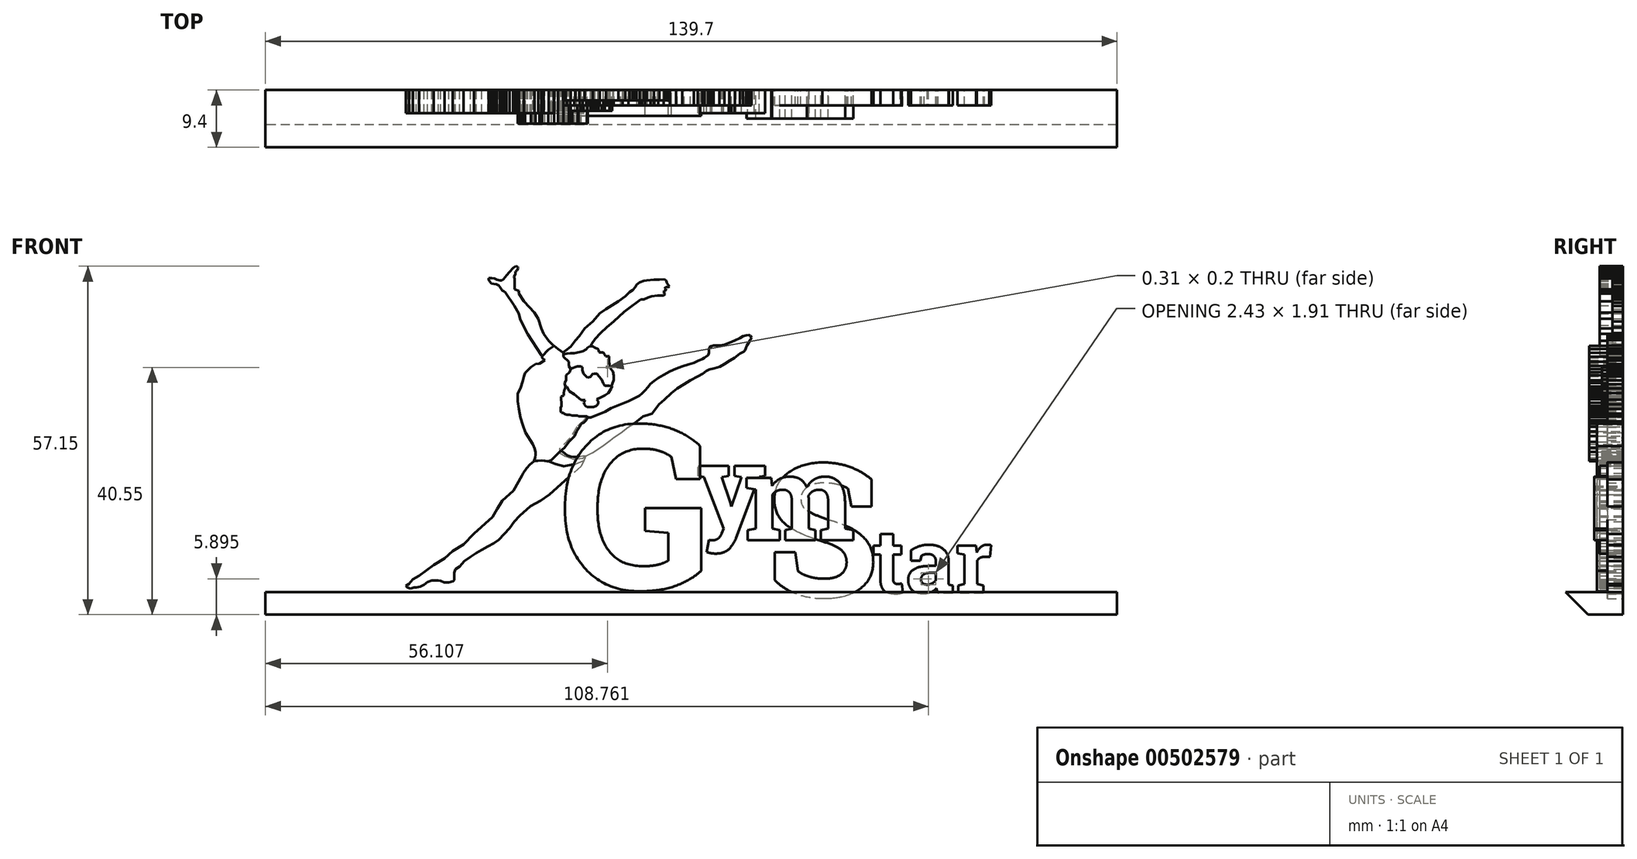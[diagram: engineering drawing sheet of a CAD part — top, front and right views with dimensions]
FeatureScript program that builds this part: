
annotation { "Feature Type Name" : "Feature", "Feature Type Description" : "" }
export const myFeature = defineFeature(function(context is Context, id is Id, definition is map)
    precondition{}
    {
        {
            var Q0;
            Q0=qCreatedBy(makeId("Front.planeOp"),FACE);
            var sketch = newSketch(context, id + "F0", { "sketchPlane" : qUnion([Q0])});
            skLineSegment(sketch, "E0", {"start": v(-43.44, 2.65) * mm, "end": v(-42.3, 3.36) * mm});
            skLineSegment(sketch, "E1", {"start": v(-42.3, 3.36) * mm, "end": v(-39.46, 5.47) * mm});
            skLineSegment(sketch, "E2", {"start": v(-39.46, 5.47) * mm, "end": v(-37.36, 6.73) * mm});
            skLineSegment(sketch, "E3", {"start": v(-37.36, 6.73) * mm, "end": v(-35.78, 8.1) * mm});
            skLineSegment(sketch, "E4", {"start": v(-35.78, 8.1) * mm, "end": v(-33.68, 9.35) * mm});
            skLineSegment(sketch, "E5", {"start": v(-33.68, 9.35) * mm, "end": v(-31.69, 11.46) * mm});
            skLineSegment(sketch, "E6", {"start": v(-31.69, 11.46) * mm, "end": v(-29.58, 13.35) * mm});
            skLineSegment(sketch, "E7", {"start": v(-29.58, 13.35) * mm, "end": v(-28.1, 14.68) * mm});
            skLineSegment(sketch, "E8", {"start": v(-28.1, 14.68) * mm, "end": v(-27.2, 16.26) * mm});
            skLineSegment(sketch, "E9", {"start": v(-27.2, 16.26) * mm, "end": v(-26.68, 17.07) * mm});
            skLineSegment(sketch, "E10", {"start": v(-26.68, 17.07) * mm, "end": v(-26.22, 17.82) * mm});
            skLineSegment(sketch, "E11", {"start": v(-26.22, 17.82) * mm, "end": v(-25.58, 18.4) * mm});
            skLineSegment(sketch, "E12", {"start": v(-25.58, 18.4) * mm, "end": v(-25.2, 18.74) * mm});
            skLineSegment(sketch, "E13", {"start": v(-25.2, 18.74) * mm, "end": v(-24.43, 19.43) * mm});
            skLineSegment(sketch, "E14", {"start": v(-24.43, 19.43) * mm, "end": v(-24.01, 19.8) * mm});
            skLineSegment(sketch, "E15", {"start": v(-24.01, 19.8) * mm, "end": v(-22.43, 22.66) * mm});
            skLineSegment(sketch, "E16", {"start": v(-22.43, 22.66) * mm, "end": v(-22.17, 23.15) * mm});
            skLineSegment(sketch, "E17", {"start": v(-22.17, 23.15) * mm, "end": v(-21.53, 24.13) * mm});
            skLineSegment(sketch, "E18", {"start": v(-21.53, 24.13) * mm, "end": v(-20.84, 24.84) * mm});
            skLineSegment(sketch, "E19", {"start": v(-20.84, 24.84) * mm, "end": v(-20.54, 25.1) * mm});
            skLineSegment(sketch, "E20", {"start": v(-20.54, 25.1) * mm, "end": v(-20.08, 25.48) * mm});
            skLineSegment(sketch, "E21", {"start": v(-20.08, 25.48) * mm, "end": v(-18.63, 25.62) * mm});
            skLineSegment(sketch, "E22", {"start": v(-18.63, 25.62) * mm, "end": v(-17.07, 25.4) * mm});
            skLineSegment(sketch, "E23", {"start": v(-17.07, 25.4) * mm, "end": v(-16, 24.93) * mm});
            skLineSegment(sketch, "E24", {"start": v(-16, 24.93) * mm, "end": v(-14.36, 24.49) * mm});
            skLineSegment(sketch, "E25", {"start": v(-14.36, 24.49) * mm, "end": v(-12.24, 24.89) * mm});
            skLineSegment(sketch, "E26", {"start": v(-12.24, 24.89) * mm, "end": v(-10.47, 25.6) * mm});
            skLineSegment(sketch, "E27", {"start": v(-10.47, 25.6) * mm, "end": v(-11, 24.49) * mm});
            skLineSegment(sketch, "E28", {"start": v(-11, 24.49) * mm, "end": v(-12.41, 23.21) * mm});
            skLineSegment(sketch, "E29", {"start": v(-12.41, 23.21) * mm, "end": v(-13.58, 22.17) * mm});
            skLineSegment(sketch, "E30", {"start": v(-13.58, 22.17) * mm, "end": v(-15.14, 20.76) * mm});
            skLineSegment(sketch, "E31", {"start": v(-15.14, 20.76) * mm, "end": v(-17.1, 19) * mm});
            skLineSegment(sketch, "E32", {"start": v(-17.1, 19) * mm, "end": v(-18.82, 17.82) * mm});
            skLineSegment(sketch, "E33", {"start": v(-18.82, 17.82) * mm, "end": v(-20.76, 16.8) * mm});
            skLineSegment(sketch, "E34", {"start": v(-20.76, 16.8) * mm, "end": v(-21.82, 15.85) * mm});
            skLineSegment(sketch, "E35", {"start": v(-21.82, 15.85) * mm, "end": v(-22.88, 14.9) * mm});
            skLineSegment(sketch, "E36", {"start": v(-22.88, 14.9) * mm, "end": v(-23.88, 13.8) * mm});
            skLineSegment(sketch, "E37", {"start": v(-23.88, 13.8) * mm, "end": v(-24.82, 12.54) * mm});
            skLineSegment(sketch, "E38", {"start": v(-24.82, 12.54) * mm, "end": v(-26.1, 11.12) * mm});
            skLineSegment(sketch, "E39", {"start": v(-26.1, 11.12) * mm, "end": v(-26.87, 10.26) * mm});
            skLineSegment(sketch, "E40", {"start": v(-26.87, 10.26) * mm, "end": v(-27.87, 9.62) * mm});
            skLineSegment(sketch, "E41", {"start": v(-27.87, 9.62) * mm, "end": v(-29, 9.01) * mm});
            skLineSegment(sketch, "E42", {"start": v(-29, 9.01) * mm, "end": v(-30.2, 8.3) * mm});
            skLineSegment(sketch, "E43", {"start": v(-30.2, 8.3) * mm, "end": v(-31.18, 7.72) * mm});
            skLineSegment(sketch, "E44", {"start": v(-31.18, 7.72) * mm, "end": v(-32.32, 6.97) * mm});
            skLineSegment(sketch, "E45", {"start": v(-32.32, 6.97) * mm, "end": v(-33.51, 6.16) * mm});
            skLineSegment(sketch, "E46", {"start": v(-33.51, 6.16) * mm, "end": v(-34.44, 5.13) * mm});
            skLineSegment(sketch, "E47", {"start": v(-34.44, 5.13) * mm, "end": v(-35.24, 4.6) * mm});
            skLineSegment(sketch, "E48", {"start": v(-35.24, 4.6) * mm, "end": v(-35.44, 3.95) * mm});
            skLineSegment(sketch, "E49", {"start": v(-35.44, 3.95) * mm, "end": v(-35.44, 3.14) * mm});
            skLineSegment(sketch, "E50", {"start": v(-35.44, 3.14) * mm, "end": v(-35.44, 2.54) * mm});
            skLineSegment(sketch, "E51", {"start": v(-35.44, 2.54) * mm, "end": v(-35.7, 2.26) * mm});
            skLineSegment(sketch, "E52", {"start": v(-35.7, 2.26) * mm, "end": v(-36.52, 2.1) * mm});
            skLineSegment(sketch, "E53", {"start": v(-36.52, 2.1) * mm, "end": v(-37.41, 2.1) * mm});
            skLineSegment(sketch, "E54", {"start": v(-37.41, 2.1) * mm, "end": v(-38.1, 2.34) * mm});
            skLineSegment(sketch, "E55", {"start": v(-38.1, 2.34) * mm, "end": v(-38.52, 2.42) * mm});
            skLineSegment(sketch, "E56", {"start": v(-38.52, 2.42) * mm, "end": v(-39.84, 2.42) * mm});
            skLineSegment(sketch, "E57", {"start": v(-39.84, 2.42) * mm, "end": v(-40.65, 2.17) * mm});
            skLineSegment(sketch, "E58", {"start": v(-40.65, 2.17) * mm, "end": v(-41.32, 1.6) * mm});
            skLineSegment(sketch, "E59", {"start": v(-41.32, 1.6) * mm, "end": v(-42.07, 1.22) * mm});
            skLineSegment(sketch, "E60", {"start": v(-42.07, 1.22) * mm, "end": v(-42.82, 1.13) * mm});
            skLineSegment(sketch, "E61", {"start": v(-42.82, 1.13) * mm, "end": v(-43.27, 1.13) * mm});
            skLineSegment(sketch, "E62", {"start": v(-43.27, 1.13) * mm, "end": v(-43.93, 0.89) * mm});
            skLineSegment(sketch, "E63", {"start": v(-43.93, 0.89) * mm, "end": v(-44.5, 1.07) * mm});
            skLineSegment(sketch, "E64", {"start": v(-44.5, 1.07) * mm, "end": v(-44.84, 1.38) * mm});
            skLineSegment(sketch, "E65", {"start": v(-44.84, 1.38) * mm, "end": v(-44.24, 1.76) * mm});
            skLineSegment(sketch, "E66", {"start": v(-44.24, 1.76) * mm, "end": v(-43.92, 2.12) * mm});
            skLineSegment(sketch, "E67", {"start": v(-43.92, 2.12) * mm, "end": v(-43.44, 2.65) * mm});
            skSolve(sketch);
        }
        {
            var Q0;
            Q0 = qSketchRegion(id + "F0", true);
            extrude(context, id + "F1", {"entities" : qUnion([Q0]), "depth" : 4.5 * mm, "offsetDistance" : 25 * mm});
        }
        {
            var Q0;
            Q0=qCreatedBy(makeId("Front.planeOp"),FACE);
            var sketch = newSketch(context, id + "F2", { "sketchPlane" : qUnion([Q0])});
            skLineSegment(sketch, "E68", {"start": v(-19.86, 26.12) * mm, "end": v(-20.1, 25.49) * mm});
            skLineSegment(sketch, "E69", {"start": v(-20.1, 25.49) * mm, "end": v(-18.62, 25.63) * mm});
            skLineSegment(sketch, "E70", {"start": v(-18.62, 25.63) * mm, "end": v(-17.22, 25.42) * mm});
            skLineSegment(sketch, "E71", {"start": v(-17.22, 25.42) * mm, "end": v(-16.72, 25.64) * mm});
            skLineSegment(sketch, "E72", {"start": v(-16.72, 25.64) * mm, "end": v(-15.68, 26.7) * mm});
            skLineSegment(sketch, "E73", {"start": v(-15.68, 26.7) * mm, "end": v(-15.16, 27.23) * mm});
            skLineSegment(sketch, "E74", {"start": v(-15.16, 27.23) * mm, "end": v(-14.2, 28.04) * mm});
            skLineSegment(sketch, "E75", {"start": v(-14.2, 28.04) * mm, "end": v(-13.4, 29.18) * mm});
            skLineSegment(sketch, "E76", {"start": v(-13.4, 29.18) * mm, "end": v(-12.27, 30.32) * mm});
            skLineSegment(sketch, "E77", {"start": v(-12.27, 30.32) * mm, "end": v(-11.84, 31.22) * mm});
            skLineSegment(sketch, "E78", {"start": v(-11.84, 31.22) * mm, "end": v(-11.3, 32.07) * mm});
            skLineSegment(sketch, "E79", {"start": v(-11.3, 32.07) * mm, "end": v(-11, 32.66) * mm});
            skLineSegment(sketch, "E80", {"start": v(-11, 32.66) * mm, "end": v(-10.47, 32.92) * mm});
            skLineSegment(sketch, "E81", {"start": v(-10.47, 32.92) * mm, "end": v(-10, 33.4) * mm});
            skLineSegment(sketch, "E82", {"start": v(-10, 33.4) * mm, "end": v(-9.71, 33.95) * mm});
            skLineSegment(sketch, "E83", {"start": v(-9.71, 33.95) * mm, "end": v(-9.86, 34.1) * mm});
            skLineSegment(sketch, "E84", {"start": v(-9.86, 34.1) * mm, "end": v(-10.68, 34.1) * mm});
            skLineSegment(sketch, "E85", {"start": v(-10.68, 34.1) * mm, "end": v(-11.46, 34.1) * mm});
            skLineSegment(sketch, "E86", {"start": v(-11.46, 34.1) * mm, "end": v(-11.6, 34.3) * mm});
            skLineSegment(sketch, "E87", {"start": v(-11.6, 34.3) * mm, "end": v(-12.13, 34.3) * mm});
            skLineSegment(sketch, "E88", {"start": v(-12.13, 34.3) * mm, "end": v(-12.65, 34.3) * mm});
            skLineSegment(sketch, "E89", {"start": v(-12.65, 34.3) * mm, "end": v(-13.18, 34.4) * mm});
            skLineSegment(sketch, "E90", {"start": v(-13.18, 34.4) * mm, "end": v(-13.7, 34.4) * mm});
            skLineSegment(sketch, "E91", {"start": v(-13.7, 34.4) * mm, "end": v(-14.15, 34.57) * mm});
            skLineSegment(sketch, "E92", {"start": v(-14.15, 34.57) * mm, "end": v(-14.38, 34.8) * mm});
            skLineSegment(sketch, "E93", {"start": v(-14.38, 34.8) * mm, "end": v(-14.77, 34.8) * mm});
            skLineSegment(sketch, "E94", {"start": v(-14.77, 34.8) * mm, "end": v(-14.91, 35.07) * mm});
            skLineSegment(sketch, "E95", {"start": v(-14.91, 35.07) * mm, "end": v(-14.91, 35.36) * mm});
            skLineSegment(sketch, "E96", {"start": v(-14.91, 35.36) * mm, "end": v(-14.97, 35.78) * mm});
            skLineSegment(sketch, "E97", {"start": v(-14.97, 35.78) * mm, "end": v(-14.76, 36.17) * mm});
            skLineSegment(sketch, "E98", {"start": v(-14.76, 36.17) * mm, "end": v(-14.76, 36.76) * mm});
            skLineSegment(sketch, "E99", {"start": v(-14.76, 36.76) * mm, "end": v(-14.88, 37.43) * mm});
            skLineSegment(sketch, "E100", {"start": v(-14.88, 37.43) * mm, "end": v(-14.88, 37.9) * mm});
            skLineSegment(sketch, "E101", {"start": v(-14.88, 37.9) * mm, "end": v(-14.37, 38.18) * mm});
            skLineSegment(sketch, "E102", {"start": v(-14.37, 38.18) * mm, "end": v(-14.32, 38.57) * mm});
            skLineSegment(sketch, "E103", {"start": v(-14.32, 38.57) * mm, "end": v(-14.3, 39.12) * mm});
            skLineSegment(sketch, "E104", {"start": v(-14.3, 39.12) * mm, "end": v(-14.12, 39.44) * mm});
            skLineSegment(sketch, "E105", {"start": v(-14.12, 39.44) * mm, "end": v(-14.04, 39.87) * mm});
            skLineSegment(sketch, "E106", {"start": v(-14.04, 39.87) * mm, "end": v(-14.18, 40.57) * mm});
            skLineSegment(sketch, "E107", {"start": v(-14.18, 40.57) * mm, "end": v(-13.85, 41.07) * mm});
            skLineSegment(sketch, "E108", {"start": v(-13.85, 41.07) * mm, "end": v(-13.85, 42.04) * mm});
            skLineSegment(sketch, "E109", {"start": v(-13.85, 42.04) * mm, "end": v(-13.2, 42.65) * mm});
            skLineSegment(sketch, "E110", {"start": v(-13.2, 42.65) * mm, "end": v(-13, 43.26) * mm});
            skLineSegment(sketch, "E111", {"start": v(-13, 43.26) * mm, "end": v(-13.35, 43.82) * mm});
            skLineSegment(sketch, "E112", {"start": v(-13.35, 43.82) * mm, "end": v(-13.35, 44.62) * mm});
            skLineSegment(sketch, "E113", {"start": v(-13.35, 44.62) * mm, "end": v(-14.41, 45.66) * mm});
            skLineSegment(sketch, "E114", {"start": v(-14.41, 45.66) * mm, "end": v(-14.41, 46.4) * mm});
            skLineSegment(sketch, "E115", {"start": v(-14.41, 46.4) * mm, "end": v(-15.48, 47.12) * mm});
            skLineSegment(sketch, "E116", {"start": v(-15.48, 47.12) * mm, "end": v(-16.2, 47.68) * mm});
            skLineSegment(sketch, "E117", {"start": v(-16.2, 47.68) * mm, "end": v(-17.3, 46.98) * mm});
            skLineSegment(sketch, "E118", {"start": v(-17.3, 46.98) * mm, "end": v(-18.52, 45.73) * mm});
            skLineSegment(sketch, "E119", {"start": v(-18.52, 45.73) * mm, "end": v(-18.52, 45.4) * mm});
            skLineSegment(sketch, "E120", {"start": v(-18.52, 45.4) * mm, "end": v(-18.03, 44.92) * mm});
            skLineSegment(sketch, "E121", {"start": v(-18.03, 44.92) * mm, "end": v(-19.03, 44.28) * mm});
            skLineSegment(sketch, "E122", {"start": v(-19.03, 44.28) * mm, "end": v(-19.82, 44.17) * mm});
            skLineSegment(sketch, "E123", {"start": v(-19.82, 44.17) * mm, "end": v(-20.68, 43.62) * mm});
            skLineSegment(sketch, "E124", {"start": v(-20.68, 43.62) * mm, "end": v(-21.27, 43.02) * mm});
            skLineSegment(sketch, "E125", {"start": v(-21.27, 43.02) * mm, "end": v(-21.82, 42.45) * mm});
            skLineSegment(sketch, "E126", {"start": v(-21.82, 42.45) * mm, "end": v(-22.03, 41.83) * mm});
            skLineSegment(sketch, "E127", {"start": v(-22.03, 41.83) * mm, "end": v(-22.26, 40.93) * mm});
            skLineSegment(sketch, "E128", {"start": v(-22.26, 40.93) * mm, "end": v(-22.68, 39.5) * mm});
            skLineSegment(sketch, "E129", {"start": v(-22.68, 39.5) * mm, "end": v(-23.19, 38.52) * mm});
            skLineSegment(sketch, "E130", {"start": v(-23.19, 38.52) * mm, "end": v(-23.19, 37.04) * mm});
            skLineSegment(sketch, "E131", {"start": v(-23.19, 37.04) * mm, "end": v(-23.03, 35.52) * mm});
            skLineSegment(sketch, "E132", {"start": v(-23.03, 35.52) * mm, "end": v(-22.68, 33.92) * mm});
            skLineSegment(sketch, "E133", {"start": v(-22.68, 33.92) * mm, "end": v(-22.26, 32.45) * mm});
            skLineSegment(sketch, "E134", {"start": v(-22.26, 32.45) * mm, "end": v(-21.73, 30.96) * mm});
            skLineSegment(sketch, "E135", {"start": v(-21.73, 30.96) * mm, "end": v(-21.13, 30.03) * mm});
            skLineSegment(sketch, "E136", {"start": v(-21.13, 30.03) * mm, "end": v(-20.32, 28.75) * mm});
            skLineSegment(sketch, "E137", {"start": v(-20.32, 28.75) * mm, "end": v(-19.97, 27.84) * mm});
            skLineSegment(sketch, "E138", {"start": v(-19.97, 27.84) * mm, "end": v(-19.78, 27.2) * mm});
            skLineSegment(sketch, "E139", {"start": v(-19.78, 27.2) * mm, "end": v(-19.78, 26.7) * mm});
            skLineSegment(sketch, "E140", {"start": v(-19.78, 26.7) * mm, "end": v(-19.86, 26.12) * mm});
            skSolve(sketch);
        }
        {
            var Q0;
            Q0 = qSketchRegion(id + "F2", true);
            extrude(context, id + "F3", {"entities" : qUnion([Q0]), "depth" : 6.5 * mm, "offsetDistance" : 25 * mm});
        }
        {
            var Q0;
            Q0=qCreatedBy(makeId("Front.planeOp"),FACE);
            var sketch = newSketch(context, id + "F4", { "sketchPlane" : qUnion([Q0])});
            skLineSegment(sketch, "E141", {"start": v(-10.44, 25.62) * mm, "end": v(-10.18, 26.15) * mm});
            skLineSegment(sketch, "E142", {"start": v(-10.18, 26.15) * mm, "end": v(-10.18, 26.4) * mm});
            skLineSegment(sketch, "E143", {"start": v(-10.18, 26.4) * mm, "end": v(-10.64, 26.4) * mm});
            skLineSegment(sketch, "E144", {"start": v(-10.64, 26.4) * mm, "end": v(-11.44, 26.25) * mm});
            skLineSegment(sketch, "E145", {"start": v(-11.44, 26.25) * mm, "end": v(-12.48, 26.25) * mm});
            skLineSegment(sketch, "E146", {"start": v(-12.48, 26.25) * mm, "end": v(-13.02, 26.35) * mm});
            skLineSegment(sketch, "E147", {"start": v(-13.02, 26.35) * mm, "end": v(-13.65, 26.6) * mm});
            skLineSegment(sketch, "E148", {"start": v(-13.65, 26.6) * mm, "end": v(-14.1, 26.98) * mm});
            skLineSegment(sketch, "E149", {"start": v(-14.1, 26.98) * mm, "end": v(-14.67, 27.36) * mm});
            skLineSegment(sketch, "E150", {"start": v(-14.67, 27.36) * mm, "end": v(-14.84, 27.5) * mm});
            skLineSegment(sketch, "E151", {"start": v(-14.84, 27.5) * mm, "end": v(-15.4, 27) * mm});
            skLineSegment(sketch, "E152", {"start": v(-15.4, 27) * mm, "end": v(-15.88, 26.48) * mm});
            skLineSegment(sketch, "E153", {"start": v(-15.88, 26.48) * mm, "end": v(-16.21, 26.2) * mm});
            skLineSegment(sketch, "E154", {"start": v(-16.21, 26.2) * mm, "end": v(-16.51, 25.86) * mm});
            skLineSegment(sketch, "E155", {"start": v(-16.51, 25.86) * mm, "end": v(-16.76, 25.65) * mm});
            skLineSegment(sketch, "E156", {"start": v(-16.76, 25.65) * mm, "end": v(-17.26, 25.43) * mm});
            skLineSegment(sketch, "E157", {"start": v(-17.26, 25.43) * mm, "end": v(-16.9, 25.29) * mm});
            skLineSegment(sketch, "E158", {"start": v(-16.9, 25.29) * mm, "end": v(-16.22, 24.96) * mm});
            skLineSegment(sketch, "E159", {"start": v(-16.22, 24.96) * mm, "end": v(-15.1, 24.62) * mm});
            skLineSegment(sketch, "E160", {"start": v(-15.1, 24.62) * mm, "end": v(-14.06, 24.47) * mm});
            skLineSegment(sketch, "E161", {"start": v(-14.06, 24.47) * mm, "end": v(-12.94, 24.64) * mm});
            skLineSegment(sketch, "E162", {"start": v(-12.94, 24.64) * mm, "end": v(-12.18, 24.84) * mm});
            skLineSegment(sketch, "E163", {"start": v(-12.18, 24.84) * mm, "end": v(-11.5, 25.14) * mm});
            skLineSegment(sketch, "E164", {"start": v(-11.5, 25.14) * mm, "end": v(-10.48, 25.57) * mm});
            skLineSegment(sketch, "E165", {"start": v(-10.44, 25.62) * mm, "end": v(-10.48, 25.57) * mm});
            skSolve(sketch);
        }
        {
            var Q0;
            Q0 = qSketchRegion(id + "F4", true);
            extrude(context, id + "F5", {"entities" : qUnion([Q0]), "depth" : 4 * mm, "offsetDistance" : 25 * mm});
        }
        {
            var Q0;
            Q0=qCreatedBy(makeId("Front.planeOp"),FACE);
            var sketch = newSketch(context, id + "F6", { "sketchPlane" : qUnion([Q0])});
            skLineSegment(sketch, "E166", {"start": v(-10.04, 26.5) * mm, "end": v(-8.77, 27.13) * mm});
            skLineSegment(sketch, "E167", {"start": v(-8.77, 27.13) * mm, "end": v(-7.76, 27.75) * mm});
            skLineSegment(sketch, "E168", {"start": v(-7.76, 27.75) * mm, "end": v(-6.54, 28.62) * mm});
            skLineSegment(sketch, "E169", {"start": v(-6.54, 28.62) * mm, "end": v(-5.36, 29.46) * mm});
            skLineSegment(sketch, "E170", {"start": v(-5.36, 29.46) * mm, "end": v(-4.62, 30.06) * mm});
            skLineSegment(sketch, "E171", {"start": v(-4.62, 30.06) * mm, "end": v(-3.31, 30.9) * mm});
            skLineSegment(sketch, "E172", {"start": v(-3.31, 30.9) * mm, "end": v(-1.95, 32.03) * mm});
            skLineSegment(sketch, "E173", {"start": v(-1.95, 32.03) * mm, "end": v(-0.18, 33.11) * mm});
            skLineSegment(sketch, "E174", {"start": v(-0.18, 33.11) * mm, "end": v(1, 34.08) * mm});
            skLineSegment(sketch, "E175", {"start": v(1, 34.08) * mm, "end": v(1.81, 34.35) * mm});
            skLineSegment(sketch, "E176", {"start": v(1.81, 34.35) * mm, "end": v(2.7, 34.66) * mm});
            skLineSegment(sketch, "E177", {"start": v(2.7, 34.66) * mm, "end": v(3.36, 35.56) * mm});
            skLineSegment(sketch, "E178", {"start": v(3.36, 35.56) * mm, "end": v(4.07, 36.45) * mm});
            skLineSegment(sketch, "E179", {"start": v(4.07, 36.45) * mm, "end": v(5.1, 37.3) * mm});
            skLineSegment(sketch, "E180", {"start": v(5.1, 37.3) * mm, "end": v(6.45, 38.61) * mm});
            skLineSegment(sketch, "E181", {"start": v(6.45, 38.61) * mm, "end": v(7.52, 39.49) * mm});
            skLineSegment(sketch, "E182", {"start": v(7.52, 39.49) * mm, "end": v(8.89, 40.32) * mm});
            skLineSegment(sketch, "E183", {"start": v(8.89, 40.32) * mm, "end": v(10.13, 41.05) * mm});
            skLineSegment(sketch, "E184", {"start": v(10.13, 41.05) * mm, "end": v(11.54, 41.79) * mm});
            skLineSegment(sketch, "E185", {"start": v(11.54, 41.79) * mm, "end": v(12.5, 42.35) * mm});
            skLineSegment(sketch, "E186", {"start": v(12.5, 42.35) * mm, "end": v(13.13, 42.87) * mm});
            skLineSegment(sketch, "E187", {"start": v(13.13, 42.87) * mm, "end": v(13.77, 43.15) * mm});
            skLineSegment(sketch, "E188", {"start": v(13.77, 43.15) * mm, "end": v(14.72, 43.37) * mm});
            skLineSegment(sketch, "E189", {"start": v(14.72, 43.37) * mm, "end": v(15.74, 43.65) * mm});
            skLineSegment(sketch, "E190", {"start": v(15.74, 43.65) * mm, "end": v(16.67, 44.2) * mm});
            skLineSegment(sketch, "E191", {"start": v(16.67, 44.2) * mm, "end": v(17.75, 44.9) * mm});
            skLineSegment(sketch, "E192", {"start": v(17.75, 44.9) * mm, "end": v(18.64, 45.37) * mm});
            skLineSegment(sketch, "E193", {"start": v(18.64, 45.37) * mm, "end": v(19.1, 45.76) * mm});
            skLineSegment(sketch, "E194", {"start": v(19.1, 45.76) * mm, "end": v(19.64, 46.2) * mm});
            skLineSegment(sketch, "E195", {"start": v(19.64, 46.2) * mm, "end": v(20.4, 46.62) * mm});
            skLineSegment(sketch, "E196", {"start": v(20.4, 46.62) * mm, "end": v(20.66, 46.83) * mm});
            skLineSegment(sketch, "E197", {"start": v(20.66, 46.83) * mm, "end": v(20.78, 47.2) * mm});
            skLineSegment(sketch, "E198", {"start": v(20.78, 47.2) * mm, "end": v(21.03, 47.8) * mm});
            skLineSegment(sketch, "E199", {"start": v(21.03, 47.8) * mm, "end": v(21.7, 48.83) * mm});
            skLineSegment(sketch, "E200", {"start": v(21.7, 48.83) * mm, "end": v(21.88, 49.3) * mm});
            skLineSegment(sketch, "E201", {"start": v(21.88, 49.3) * mm, "end": v(21.7, 49.63) * mm});
            skLineSegment(sketch, "E202", {"start": v(21.7, 49.63) * mm, "end": v(21.38, 49.78) * mm});
            skLineSegment(sketch, "E203", {"start": v(21.38, 49.78) * mm, "end": v(20.84, 49.76) * mm});
            skLineSegment(sketch, "E204", {"start": v(20.84, 49.76) * mm, "end": v(20.24, 49.6) * mm});
            skLineSegment(sketch, "E205", {"start": v(20.24, 49.6) * mm, "end": v(19.65, 49.19) * mm});
            skLineSegment(sketch, "E206", {"start": v(19.65, 49.19) * mm, "end": v(18.66, 48.8) * mm});
            skLineSegment(sketch, "E207", {"start": v(18.66, 48.8) * mm, "end": v(17.68, 48.32) * mm});
            skLineSegment(sketch, "E208", {"start": v(17.68, 48.32) * mm, "end": v(16.7, 47.94) * mm});
            skLineSegment(sketch, "E209", {"start": v(16.7, 47.94) * mm, "end": v(15.7, 47.8) * mm});
            skLineSegment(sketch, "E210", {"start": v(15.7, 47.8) * mm, "end": v(15.05, 47.8) * mm});
            skLineSegment(sketch, "E211", {"start": v(15.05, 47.8) * mm, "end": v(14.56, 47.8) * mm});
            skLineSegment(sketch, "E212", {"start": v(14.56, 47.8) * mm, "end": v(14.1, 47.68) * mm});
            skLineSegment(sketch, "E213", {"start": v(14.1, 47.68) * mm, "end": v(13.77, 47.4) * mm});
            skLineSegment(sketch, "E214", {"start": v(13.77, 47.4) * mm, "end": v(13.67, 47) * mm});
            skLineSegment(sketch, "E215", {"start": v(13.67, 47) * mm, "end": v(13.68, 46.4) * mm});
            skLineSegment(sketch, "E216", {"start": v(13.68, 46.4) * mm, "end": v(13.5, 45.89) * mm});
            skLineSegment(sketch, "E217", {"start": v(13.5, 45.89) * mm, "end": v(12.79, 45.43) * mm});
            skLineSegment(sketch, "E218", {"start": v(12.79, 45.43) * mm, "end": v(12.43, 45.2) * mm});
            skLineSegment(sketch, "E219", {"start": v(12.43, 45.2) * mm, "end": v(11.54, 44.78) * mm});
            skLineSegment(sketch, "E220", {"start": v(11.54, 44.78) * mm, "end": v(10.77, 44.44) * mm});
            skLineSegment(sketch, "E221", {"start": v(10.77, 44.44) * mm, "end": v(9.71, 44.13) * mm});
            skLineSegment(sketch, "E222", {"start": v(9.71, 44.13) * mm, "end": v(8.53, 43.77) * mm});
            skLineSegment(sketch, "E223", {"start": v(8.53, 43.77) * mm, "end": v(7.3, 43.34) * mm});
            skLineSegment(sketch, "E224", {"start": v(7.3, 43.34) * mm, "end": v(6.1, 42.76) * mm});
            skLineSegment(sketch, "E225", {"start": v(6.1, 42.76) * mm, "end": v(4.92, 42.1) * mm});
            skLineSegment(sketch, "E226", {"start": v(4.92, 42.1) * mm, "end": v(3.92, 41.49) * mm});
            skLineSegment(sketch, "E227", {"start": v(3.92, 41.49) * mm, "end": v(3.08, 40.9) * mm});
            skLineSegment(sketch, "E228", {"start": v(3.08, 40.9) * mm, "end": v(2.4, 40.36) * mm});
            skLineSegment(sketch, "E229", {"start": v(2.4, 40.36) * mm, "end": v(1.87, 39.74) * mm});
            skLineSegment(sketch, "E230", {"start": v(1.87, 39.74) * mm, "end": v(1.32, 39.1) * mm});
            skLineSegment(sketch, "E231", {"start": v(1.32, 39.1) * mm, "end": v(0.77, 38.52) * mm});
            skLineSegment(sketch, "E232", {"start": v(0.77, 38.52) * mm, "end": v(0.25, 38.1) * mm});
            skLineSegment(sketch, "E233", {"start": v(0.25, 38.1) * mm, "end": v(-1.89, 37.02) * mm});
            skLineSegment(sketch, "E234", {"start": v(-1.89, 37.02) * mm, "end": v(-3, 36.61) * mm});
            skLineSegment(sketch, "E235", {"start": v(-3, 36.61) * mm, "end": v(-4.25, 36.09) * mm});
            skLineSegment(sketch, "E236", {"start": v(-4.25, 36.09) * mm, "end": v(-5.19, 35.7) * mm});
            skLineSegment(sketch, "E237", {"start": v(-5.19, 35.7) * mm, "end": v(-6.32, 35.01) * mm});
            skLineSegment(sketch, "E238", {"start": v(-6.32, 35.01) * mm, "end": v(-7.47, 34.53) * mm});
            skLineSegment(sketch, "E239", {"start": v(-7.47, 34.53) * mm, "end": v(-8.22, 34.22) * mm});
            skLineSegment(sketch, "E240", {"start": v(-8.22, 34.22) * mm, "end": v(-9.08, 33.86) * mm});
            skLineSegment(sketch, "E241", {"start": v(-9.08, 33.86) * mm, "end": v(-9.87, 33.86) * mm});
            skLineSegment(sketch, "E242", {"start": v(-9.87, 33.86) * mm, "end": v(-10.32, 33.5) * mm});
            skLineSegment(sketch, "E243", {"start": v(-10.32, 33.5) * mm, "end": v(-11.77, 32.13) * mm});
            skLineSegment(sketch, "E244", {"start": v(-11.77, 32.13) * mm, "end": v(-13.13, 29.97) * mm});
            skLineSegment(sketch, "E245", {"start": v(-13.13, 29.97) * mm, "end": v(-15.12, 27.85) * mm});
            skLineSegment(sketch, "E246", {"start": v(-15.12, 27.85) * mm, "end": v(-15.12, 27.13) * mm});
            skLineSegment(sketch, "E247", {"start": v(-15.12, 27.13) * mm, "end": v(-14, 26.42) * mm});
            skLineSegment(sketch, "E248", {"start": v(-14, 26.42) * mm, "end": v(-12.38, 25.83) * mm});
            skLineSegment(sketch, "E249", {"start": v(-12.38, 25.83) * mm, "end": v(-10.64, 26.05) * mm});
            skLineSegment(sketch, "E250", {"start": v(-10.64, 26.05) * mm, "end": v(-10.04, 26.5) * mm});
            skSolve(sketch);
        }
        {
            var Q0;
            Q0 = qSketchRegion(id + "F6", true);
            extrude(context, id + "F7", {"entities" : qUnion([Q0]), "depth" : 3 * mm, "offsetDistance" : 25 * mm});
        }
        {
            var Q0;
            Q0=qCreatedBy(makeId("Front.planeOp"),FACE);
            var sketch = newSketch(context, id + "F8", { "sketchPlane" : qUnion([Q0])});
            skLineSegment(sketch, "E251", {"start": v(-14.23, 39.87) * mm, "end": v(-13.7, 39.87) * mm});
            skLineSegment(sketch, "E252", {"start": v(-13.7, 39.87) * mm, "end": v(-13.3, 39) * mm});
            skLineSegment(sketch, "E253", {"start": v(-13.3, 39) * mm, "end": v(-12.32, 38.36) * mm});
            skLineSegment(sketch, "E254", {"start": v(-12.32, 38.36) * mm, "end": v(-11.4, 37.64) * mm});
            skLineSegment(sketch, "E255", {"start": v(-11.4, 37.64) * mm, "end": v(-10.96, 37.25) * mm});
            skLineSegment(sketch, "E256", {"start": v(-10.96, 37.25) * mm, "end": v(-10.2, 37.28) * mm});
            skLineSegment(sketch, "E257", {"start": v(-10.2, 37.28) * mm, "end": v(-10.46, 36.8) * mm});
            skLineSegment(sketch, "E258", {"start": v(-10.46, 36.8) * mm, "end": v(-10.4, 36.46) * mm});
            skLineSegment(sketch, "E259", {"start": v(-10.4, 36.46) * mm, "end": v(-10.12, 36.15) * mm});
            skLineSegment(sketch, "E260", {"start": v(-10.12, 36.15) * mm, "end": v(-9.84, 35.9) * mm});
            skLineSegment(sketch, "E261", {"start": v(-9.84, 35.9) * mm, "end": v(-9.22, 35.9) * mm});
            skLineSegment(sketch, "E262", {"start": v(-9.22, 35.9) * mm, "end": v(-8.55, 35.9) * mm});
            skLineSegment(sketch, "E263", {"start": v(-8.55, 35.9) * mm, "end": v(-8.1, 36.15) * mm});
            skLineSegment(sketch, "E264", {"start": v(-8.1, 36.15) * mm, "end": v(-7.77, 36.46) * mm});
            skLineSegment(sketch, "E265", {"start": v(-7.77, 36.46) * mm, "end": v(-7.68, 36.71) * mm});
            skLineSegment(sketch, "E266", {"start": v(-7.68, 36.71) * mm, "end": v(-7.68, 37.05) * mm});
            skLineSegment(sketch, "E267", {"start": v(-7.68, 37.05) * mm, "end": v(-7.98, 37.39) * mm});
            skLineSegment(sketch, "E268", {"start": v(-7.98, 37.39) * mm, "end": v(-7.14, 37.76) * mm});
            skLineSegment(sketch, "E269", {"start": v(-7.14, 37.76) * mm, "end": v(-6.4, 38.12) * mm});
            skLineSegment(sketch, "E270", {"start": v(-6.4, 38.12) * mm, "end": v(-5.75, 38.6) * mm});
            skLineSegment(sketch, "E271", {"start": v(-5.75, 38.6) * mm, "end": v(-5.2, 39.4) * mm});
            skLineSegment(sketch, "E272", {"start": v(-5.2, 39.4) * mm, "end": v(-4.97, 39.94) * mm});
            skLineSegment(sketch, "E273", {"start": v(-4.97, 39.94) * mm, "end": v(-5.55, 40.04) * mm});
            skLineSegment(sketch, "E274", {"start": v(-5.55, 40.04) * mm, "end": v(-6.4, 40.04) * mm});
            skLineSegment(sketch, "E275", {"start": v(-6.4, 40.04) * mm, "end": v(-6.73, 40.44) * mm});
            skLineSegment(sketch, "E276", {"start": v(-6.73, 40.44) * mm, "end": v(-7, 41.25) * mm});
            skLineSegment(sketch, "E277", {"start": v(-7, 41.25) * mm, "end": v(-7.62, 41.87) * mm});
            skLineSegment(sketch, "E278", {"start": v(-7.62, 41.87) * mm, "end": v(-7.87, 42.35) * mm});
            skLineSegment(sketch, "E279", {"start": v(-7.87, 42.35) * mm, "end": v(-8.4, 42.35) * mm});
            skLineSegment(sketch, "E280", {"start": v(-8.4, 42.35) * mm, "end": v(-8.8, 42.26) * mm});
            skLineSegment(sketch, "E281", {"start": v(-8.8, 42.26) * mm, "end": v(-9.2, 41.73) * mm});
            skLineSegment(sketch, "E282", {"start": v(-9.2, 41.73) * mm, "end": v(-9.75, 41.62) * mm});
            skLineSegment(sketch, "E283", {"start": v(-9.75, 41.62) * mm, "end": v(-10.5, 42.32) * mm});
            skLineSegment(sketch, "E284", {"start": v(-10.5, 42.32) * mm, "end": v(-10.75, 43) * mm});
            skLineSegment(sketch, "E285", {"start": v(-10.75, 43) * mm, "end": v(-10.75, 43.64) * mm});
            skLineSegment(sketch, "E286", {"start": v(-10.75, 43.64) * mm, "end": v(-11.1, 43.78) * mm});
            skLineSegment(sketch, "E287", {"start": v(-11.1, 43.78) * mm, "end": v(-11.72, 43.78) * mm});
            skLineSegment(sketch, "E288", {"start": v(-11.72, 43.78) * mm, "end": v(-12.58, 43.45) * mm});
            skLineSegment(sketch, "E289", {"start": v(-12.58, 43.45) * mm, "end": v(-13.2, 43.23) * mm});
            skLineSegment(sketch, "E290", {"start": v(-13.2, 43.23) * mm, "end": v(-13.98, 42.47) * mm});
            skLineSegment(sketch, "E291", {"start": v(-13.98, 42.47) * mm, "end": v(-14.28, 41.77) * mm});
            skLineSegment(sketch, "E292", {"start": v(-14.28, 41.77) * mm, "end": v(-14.7, 40.53) * mm});
            skLineSegment(sketch, "E293", {"start": v(-14.7, 40.53) * mm, "end": v(-14.5, 39.99) * mm});
            skLineSegment(sketch, "E294", {"start": v(-14.5, 39.99) * mm, "end": v(-14.23, 39.87) * mm});
            skSolve(sketch);
        }
        {
            var Q0;
            Q0 = qSketchRegion(id + "F8", true);
            extrude(context, id + "F9", {"entities" : qUnion([Q0]), "operationType" : NewBodyOperationType.ADD, "depth" : 4 * mm, "offsetDistance" : 25 * mm});
        }
        {
            var Q0;
            Q0=qCreatedBy(makeId("Front.planeOp"),FACE);
            var sketch = newSketch(context, id + "F10", { "sketchPlane" : qUnion([Q0])});
            skLineSegment(sketch, "E295", {"start": v(-5.28, 39.8) * mm, "end": v(-4.97, 40.33) * mm});
            skLineSegment(sketch, "E296", {"start": v(-4.97, 40.33) * mm, "end": v(-4.7, 41.14) * mm});
            skLineSegment(sketch, "E297", {"start": v(-4.7, 41.14) * mm, "end": v(-4.7, 41.93) * mm});
            skLineSegment(sketch, "E298", {"start": v(-4.7, 41.93) * mm, "end": v(-4.8, 42.8) * mm});
            skLineSegment(sketch, "E299", {"start": v(-4.8, 42.8) * mm, "end": v(-5.33, 43.35) * mm});
            skLineSegment(sketch, "E300", {"start": v(-5.33, 43.35) * mm, "end": v(-5.62, 44.74) * mm});
            skLineSegment(sketch, "E301", {"start": v(-5.62, 44.74) * mm, "end": v(-5.62, 45.54) * mm});
            skLineSegment(sketch, "E302", {"start": v(-5.62, 45.54) * mm, "end": v(-5.62, 45.7) * mm});
            skLineSegment(sketch, "E303", {"start": v(-5.62, 45.7) * mm, "end": v(-5.82, 45.8) * mm});
            skLineSegment(sketch, "E304", {"start": v(-5.82, 45.8) * mm, "end": v(-6, 45.7) * mm});
            skLineSegment(sketch, "E305", {"start": v(-6, 45.7) * mm, "end": v(-6.15, 45.7) * mm});
            skLineSegment(sketch, "E306", {"start": v(-6.15, 45.7) * mm, "end": v(-6.26, 45.7) * mm});
            skLineSegment(sketch, "E307", {"start": v(-6.26, 45.7) * mm, "end": v(-6.45, 46) * mm});
            skLineSegment(sketch, "E308", {"start": v(-6.45, 46) * mm, "end": v(-6.57, 46.2) * mm});
            skLineSegment(sketch, "E309", {"start": v(-6.57, 46.2) * mm, "end": v(-6.7, 46.41) * mm});
            skLineSegment(sketch, "E310", {"start": v(-6.7, 46.41) * mm, "end": v(-7.07, 46.41) * mm});
            skLineSegment(sketch, "E311", {"start": v(-7.07, 46.41) * mm, "end": v(-7.36, 46.41) * mm});
            skLineSegment(sketch, "E312", {"start": v(-7.36, 46.41) * mm, "end": v(-7.56, 46.53) * mm});
            skLineSegment(sketch, "E313", {"start": v(-7.56, 46.53) * mm, "end": v(-7.62, 46.86) * mm});
            skLineSegment(sketch, "E314", {"start": v(-7.62, 46.86) * mm, "end": v(-7.78, 47.13) * mm});
            skLineSegment(sketch, "E315", {"start": v(-7.78, 47.13) * mm, "end": v(-8.28, 47.34) * mm});
            skLineSegment(sketch, "E316", {"start": v(-8.28, 47.34) * mm, "end": v(-8.8, 47.6) * mm});
            skLineSegment(sketch, "E317", {"start": v(-8.8, 47.6) * mm, "end": v(-9.3, 47.6) * mm});
            skLineSegment(sketch, "E318", {"start": v(-9.3, 47.6) * mm, "end": v(-9.4, 47.54) * mm});
            skLineSegment(sketch, "E319", {"start": v(-9.4, 47.54) * mm, "end": v(-9.76, 47.33) * mm});
            skLineSegment(sketch, "E320", {"start": v(-9.76, 47.33) * mm, "end": v(-10.02, 47.06) * mm});
            skLineSegment(sketch, "E321", {"start": v(-10.02, 47.06) * mm, "end": v(-10.67, 46.66) * mm});
            skLineSegment(sketch, "E322", {"start": v(-10.67, 46.66) * mm, "end": v(-11.24, 46.5) * mm});
            skLineSegment(sketch, "E323", {"start": v(-11.24, 46.5) * mm, "end": v(-12.34, 46.3) * mm});
            skLineSegment(sketch, "E324", {"start": v(-12.34, 46.3) * mm, "end": v(-13.08, 46.3) * mm});
            skLineSegment(sketch, "E325", {"start": v(-13.08, 46.3) * mm, "end": v(-13.74, 46.2) * mm});
            skLineSegment(sketch, "E326", {"start": v(-13.74, 46.2) * mm, "end": v(-14.63, 46.03) * mm});
            skLineSegment(sketch, "E327", {"start": v(-14.63, 46.03) * mm, "end": v(-14.38, 43.8) * mm});
            skLineSegment(sketch, "E328", {"start": v(-14.38, 43.8) * mm, "end": v(-13.54, 43.17) * mm});
            skLineSegment(sketch, "E329", {"start": v(-13.54, 43.17) * mm, "end": v(-11.12, 41.5) * mm});
            skLineSegment(sketch, "E330", {"start": v(-11.12, 41.5) * mm, "end": v(-8.48, 41.13) * mm});
            skLineSegment(sketch, "E331", {"start": v(-8.48, 41.13) * mm, "end": v(-6.76, 39.6) * mm});
            skLineSegment(sketch, "E332", {"start": v(-6.76, 39.6) * mm, "end": v(-5.28, 39.8) * mm});
            skLineSegment(sketch, "E333", {"start": v(-6.1, 43.64) * mm, "end": v(-5.97, 43.43) * mm});
            skLineSegment(sketch, "E334", {"start": v(-5.97, 43.43) * mm, "end": v(-5.8, 43.53) * mm});
            skLineSegment(sketch, "E335", {"start": v(-5.8, 43.53) * mm, "end": v(-5.73, 43.66) * mm});
            skLineSegment(sketch, "E336", {"start": v(-5.73, 43.66) * mm, "end": v(-6.1, 43.64) * mm});
            skSolve(sketch);
        }
        {
            var Q0;
            Q0 = qSketchRegion(id + "F10", true);
            extrude(context, id + "F11", {"entities" : qUnion([Q0]), "operationType" : NewBodyOperationType.ADD, "depth" : 3 * mm, "offsetDistance" : 25 * mm});
        }
        {
            var Q0;
            Q0=qCreatedBy(makeId("Front.planeOp"),FACE);
            var sketch = newSketch(context, id + "F12", { "sketchPlane" : qUnion([Q0])});
            skLineSegment(sketch, "E337", {"start": v(-9.59, 46.9) * mm, "end": v(-8.97, 48.05) * mm});
            skLineSegment(sketch, "E338", {"start": v(-8.97, 48.05) * mm, "end": v(-8.25, 49.04) * mm});
            skLineSegment(sketch, "E339", {"start": v(-8.25, 49.04) * mm, "end": v(-7.2, 50.17) * mm});
            skLineSegment(sketch, "E340", {"start": v(-7.2, 50.17) * mm, "end": v(-6.06, 51.27) * mm});
            skLineSegment(sketch, "E341", {"start": v(-6.06, 51.27) * mm, "end": v(-4.66, 52.44) * mm});
            skLineSegment(sketch, "E342", {"start": v(-4.66, 52.44) * mm, "end": v(-2.67, 54.3) * mm});
            skLineSegment(sketch, "E343", {"start": v(-2.67, 54.3) * mm, "end": v(-1.19, 55.4) * mm});
            skLineSegment(sketch, "E344", {"start": v(-1.19, 55.4) * mm, "end": v(-0.33, 56.02) * mm});
            skLineSegment(sketch, "E345", {"start": v(-0.33, 56.02) * mm, "end": v(0.57, 56.7) * mm});
            skLineSegment(sketch, "E346", {"start": v(0.57, 56.7) * mm, "end": v(1.1, 56.7) * mm});
            skLineSegment(sketch, "E347", {"start": v(1.1, 56.7) * mm, "end": v(1.97, 57.04) * mm});
            skLineSegment(sketch, "E348", {"start": v(1.97, 57.04) * mm, "end": v(2.6, 57.25) * mm});
            skLineSegment(sketch, "E349", {"start": v(2.6, 57.25) * mm, "end": v(3.78, 57.46) * mm});
            skLineSegment(sketch, "E350", {"start": v(3.78, 57.46) * mm, "end": v(4.9, 57.46) * mm});
            skLineSegment(sketch, "E351", {"start": v(4.9, 57.46) * mm, "end": v(5.22, 57.69) * mm});
            skLineSegment(sketch, "E352", {"start": v(5.22, 57.69) * mm, "end": v(4.9, 58.12) * mm});
            skLineSegment(sketch, "E353", {"start": v(4.9, 58.12) * mm, "end": v(5.39, 58.49) * mm});
            skLineSegment(sketch, "E354", {"start": v(5.39, 58.49) * mm, "end": v(5.39, 58.66) * mm});
            skLineSegment(sketch, "E355", {"start": v(5.39, 58.66) * mm, "end": v(5.06, 58.8) * mm});
            skLineSegment(sketch, "E356", {"start": v(5.06, 58.8) * mm, "end": v(5.39, 59.05) * mm});
            skLineSegment(sketch, "E357", {"start": v(5.39, 59.05) * mm, "end": v(5.92, 59.05) * mm});
            skLineSegment(sketch, "E358", {"start": v(5.92, 59.05) * mm, "end": v(6.1, 59.18) * mm});
            skLineSegment(sketch, "E359", {"start": v(6.1, 59.18) * mm, "end": v(5.9, 59.43) * mm});
            skLineSegment(sketch, "E360", {"start": v(5.9, 59.43) * mm, "end": v(5.57, 59.89) * mm});
            skLineSegment(sketch, "E361", {"start": v(5.57, 59.89) * mm, "end": v(5.49, 60.27) * mm});
            skLineSegment(sketch, "E362", {"start": v(5.49, 60.27) * mm, "end": v(5.09, 60.58) * mm});
            skLineSegment(sketch, "E363", {"start": v(5.09, 60.58) * mm, "end": v(4.11, 60.5) * mm});
            skLineSegment(sketch, "E364", {"start": v(4.11, 60.5) * mm, "end": v(3.06, 60.5) * mm});
            skLineSegment(sketch, "E365", {"start": v(3.06, 60.5) * mm, "end": v(1.66, 60.35) * mm});
            skLineSegment(sketch, "E366", {"start": v(1.66, 60.35) * mm, "end": v(1.17, 60.25) * mm});
            skLineSegment(sketch, "E367", {"start": v(1.17, 60.25) * mm, "end": v(0.28, 59.96) * mm});
            skLineSegment(sketch, "E368", {"start": v(0.28, 59.96) * mm, "end": v(-0.27, 59.5) * mm});
            skLineSegment(sketch, "E369", {"start": v(-0.27, 59.5) * mm, "end": v(-0.52, 59.03) * mm});
            skLineSegment(sketch, "E370", {"start": v(-0.52, 59.03) * mm, "end": v(-1.04, 58.49) * mm});
            skLineSegment(sketch, "E371", {"start": v(-1.04, 58.49) * mm, "end": v(-1.6, 58.06) * mm});
            skLineSegment(sketch, "E372", {"start": v(-1.6, 58.06) * mm, "end": v(-2.49, 57.3) * mm});
            skLineSegment(sketch, "E373", {"start": v(-2.49, 57.3) * mm, "end": v(-3.82, 56.3) * mm});
            skLineSegment(sketch, "E374", {"start": v(-3.82, 56.3) * mm, "end": v(-6.18, 54.84) * mm});
            skLineSegment(sketch, "E375", {"start": v(-6.18, 54.84) * mm, "end": v(-7.4, 53.96) * mm});
            skLineSegment(sketch, "E376", {"start": v(-7.4, 53.96) * mm, "end": v(-8.72, 52.44) * mm});
            skLineSegment(sketch, "E377", {"start": v(-8.72, 52.44) * mm, "end": v(-10.3, 51.04) * mm});
            skLineSegment(sketch, "E378", {"start": v(-10.3, 51.04) * mm, "end": v(-11.35, 49.6) * mm});
            skLineSegment(sketch, "E379", {"start": v(-11.35, 49.6) * mm, "end": v(-12.08, 48.77) * mm});
            skLineSegment(sketch, "E380", {"start": v(-12.08, 48.77) * mm, "end": v(-13, 47.54) * mm});
            skLineSegment(sketch, "E381", {"start": v(-13, 47.54) * mm, "end": v(-13.93, 46.85) * mm});
            skLineSegment(sketch, "E382", {"start": v(-13.93, 46.85) * mm, "end": v(-15, 46.07) * mm});
            skLineSegment(sketch, "E383", {"start": v(-15, 46.07) * mm, "end": v(-14.5, 45.13) * mm});
            skLineSegment(sketch, "E384", {"start": v(-14.5, 45.13) * mm, "end": v(-11.7, 45.38) * mm});
            skLineSegment(sketch, "E385", {"start": v(-11.7, 45.38) * mm, "end": v(-9.58, 46.07) * mm});
            skLineSegment(sketch, "E386", {"start": v(-9.58, 46.07) * mm, "end": v(-9.59, 46.9) * mm});
            skSolve(sketch);
        }
        {
            var Q0;
            Q0 = qSketchRegion(id + "F12", true);
            extrude(context, id + "F13", {"entities" : qUnion([Q0]), "operationType" : NewBodyOperationType.ADD, "depth" : 2 * mm, "offsetDistance" : 25 * mm});
        }
        {
            var Q0;
            Q0=qCreatedBy(makeId("Front.planeOp"),FACE);
            var sketch = newSketch(context, id + "F14", { "sketchPlane" : qUnion([Q0])});
            skLineSegment(sketch, "E387", {"start": v(-16.25, 47.72) * mm, "end": v(-17.22, 48.7) * mm});
            skLineSegment(sketch, "E388", {"start": v(-17.22, 48.7) * mm, "end": v(-18.22, 50.04) * mm});
            skLineSegment(sketch, "E389", {"start": v(-18.22, 50.04) * mm, "end": v(-18.68, 51.1) * mm});
            skLineSegment(sketch, "E390", {"start": v(-18.68, 51.1) * mm, "end": v(-19.28, 52.91) * mm});
            skLineSegment(sketch, "E391", {"start": v(-19.28, 52.91) * mm, "end": v(-20.03, 54.17) * mm});
            skLineSegment(sketch, "E392", {"start": v(-20.03, 54.17) * mm, "end": v(-22, 56.3) * mm});
            skLineSegment(sketch, "E393", {"start": v(-22, 56.3) * mm, "end": v(-22.97, 57.77) * mm});
            skLineSegment(sketch, "E394", {"start": v(-22.97, 57.77) * mm, "end": v(-22.97, 58.33) * mm});
            skLineSegment(sketch, "E395", {"start": v(-22.97, 58.33) * mm, "end": v(-23.81, 58.64) * mm});
            skLineSegment(sketch, "E396", {"start": v(-23.81, 58.64) * mm, "end": v(-23.81, 59.7) * mm});
            skLineSegment(sketch, "E397", {"start": v(-23.81, 59.7) * mm, "end": v(-23.81, 60.47) * mm});
            skLineSegment(sketch, "E398", {"start": v(-23.81, 60.47) * mm, "end": v(-23.81, 60.74) * mm});
            skLineSegment(sketch, "E399", {"start": v(-23.81, 60.74) * mm, "end": v(-24, 61.02) * mm});
            skLineSegment(sketch, "E400", {"start": v(-24, 61.02) * mm, "end": v(-23.68, 61.53) * mm});
            skLineSegment(sketch, "E401", {"start": v(-23.68, 61.53) * mm, "end": v(-23.68, 62.04) * mm});
            skLineSegment(sketch, "E402", {"start": v(-23.68, 62.04) * mm, "end": v(-23.37, 62.24) * mm});
            skLineSegment(sketch, "E403", {"start": v(-23.37, 62.24) * mm, "end": v(-23.15, 62.7) * mm});
            skLineSegment(sketch, "E404", {"start": v(-23.15, 62.7) * mm, "end": v(-23.2, 62.92) * mm});
            skLineSegment(sketch, "E405", {"start": v(-23.2, 62.92) * mm, "end": v(-23.56, 63.08) * mm});
            skLineSegment(sketch, "E406", {"start": v(-23.56, 63.08) * mm, "end": v(-24.12, 62.71) * mm});
            skLineSegment(sketch, "E407", {"start": v(-24.12, 62.71) * mm, "end": v(-24.78, 62) * mm});
            skLineSegment(sketch, "E408", {"start": v(-24.78, 62) * mm, "end": v(-25.38, 61.3) * mm});
            skLineSegment(sketch, "E409", {"start": v(-25.38, 61.3) * mm, "end": v(-25.64, 60.98) * mm});
            skLineSegment(sketch, "E410", {"start": v(-25.64, 60.98) * mm, "end": v(-26, 60.6) * mm});
            skLineSegment(sketch, "E411", {"start": v(-26, 60.6) * mm, "end": v(-26.25, 60.36) * mm});
            skLineSegment(sketch, "E412", {"start": v(-26.25, 60.36) * mm, "end": v(-26.67, 60.36) * mm});
            skLineSegment(sketch, "E413", {"start": v(-26.67, 60.36) * mm, "end": v(-27.27, 60.47) * mm});
            skLineSegment(sketch, "E414", {"start": v(-27.27, 60.47) * mm, "end": v(-27.73, 60.68) * mm});
            skLineSegment(sketch, "E415", {"start": v(-27.73, 60.68) * mm, "end": v(-28.24, 60.8) * mm});
            skLineSegment(sketch, "E416", {"start": v(-28.24, 60.8) * mm, "end": v(-28.65, 60.8) * mm});
            skLineSegment(sketch, "E417", {"start": v(-28.65, 60.8) * mm, "end": v(-28.8, 60.75) * mm});
            skLineSegment(sketch, "E418", {"start": v(-28.8, 60.75) * mm, "end": v(-28.8, 60.47) * mm});
            skLineSegment(sketch, "E419", {"start": v(-28.8, 60.47) * mm, "end": v(-28.65, 60.2) * mm});
            skLineSegment(sketch, "E420", {"start": v(-28.65, 60.2) * mm, "end": v(-28.28, 59.75) * mm});
            skLineSegment(sketch, "E421", {"start": v(-28.28, 59.75) * mm, "end": v(-27.87, 59.67) * mm});
            skLineSegment(sketch, "E422", {"start": v(-27.87, 59.67) * mm, "end": v(-27.34, 59.56) * mm});
            skLineSegment(sketch, "E423", {"start": v(-27.34, 59.56) * mm, "end": v(-26.9, 59.38) * mm});
            skLineSegment(sketch, "E424", {"start": v(-26.9, 59.38) * mm, "end": v(-26.68, 59.07) * mm});
            skLineSegment(sketch, "E425", {"start": v(-26.68, 59.07) * mm, "end": v(-26.23, 58.4) * mm});
            skLineSegment(sketch, "E426", {"start": v(-26.23, 58.4) * mm, "end": v(-25.94, 58.25) * mm});
            skLineSegment(sketch, "E427", {"start": v(-25.94, 58.25) * mm, "end": v(-25.58, 58.05) * mm});
            skLineSegment(sketch, "E428", {"start": v(-25.58, 58.05) * mm, "end": v(-25.4, 57.77) * mm});
            skLineSegment(sketch, "E429", {"start": v(-25.4, 57.77) * mm, "end": v(-24.8, 56.87) * mm});
            skLineSegment(sketch, "E430", {"start": v(-24.8, 56.87) * mm, "end": v(-23.9, 55.5) * mm});
            skLineSegment(sketch, "E431", {"start": v(-23.9, 55.5) * mm, "end": v(-22.97, 53.94) * mm});
            skLineSegment(sketch, "E432", {"start": v(-22.97, 53.94) * mm, "end": v(-22.74, 52.92) * mm});
            skLineSegment(sketch, "E433", {"start": v(-22.74, 52.92) * mm, "end": v(-22.2, 51.67) * mm});
            skLineSegment(sketch, "E434", {"start": v(-22.2, 51.67) * mm, "end": v(-21.32, 49.98) * mm});
            skLineSegment(sketch, "E435", {"start": v(-21.32, 49.98) * mm, "end": v(-18.65, 45.93) * mm});
            skLineSegment(sketch, "E436", {"start": v(-18.65, 45.93) * mm, "end": v(-18.3, 45.55) * mm});
            skLineSegment(sketch, "E437", {"start": v(-18.3, 45.55) * mm, "end": v(-16.04, 46.8) * mm});
            skLineSegment(sketch, "E438", {"start": v(-16.04, 46.8) * mm, "end": v(-16.25, 47.72) * mm});
            skSolve(sketch);
        }
        {
            var Q0;
            Q0 = qSketchRegion(id + "F14", true);
            extrude(context, id + "F15", {"entities" : qUnion([Q0]), "operationType" : NewBodyOperationType.ADD, "depth" : 4.5 * mm, "offsetDistance" : 25 * mm});
        }
        {
            var Q0;
            Q0=qCreatedBy(makeId("Front.planeOp"),FACE);
            var sketch = newSketch(context, id + "F16", { "sketchPlane" : qUnion([Q0])});
            skText(sketch, "E439", { "text": "G", "fontName": "RobotoSlab-Bold.ttf"});
            const initialGuessF16  = {"E439": [0, 0.00692, 1, 0, 0.03186]};
            skSetInitialGuess(sketch, initialGuessF16);
            skSolve(sketch);
        }
        {
            var Q0;
            Q0 = qSketchRegion(id + "F16", true);
            extrude(context, id + "F17", {"entities" : qUnion([Q0]), "depth" : 5 * mm, "offsetDistance" : 25 * mm});
        }
        {
            var Q0;
            Q0=makeQuery(id+"F17.opExtrude","SWEPT_BODY",BODY,{"disambiguationData":[OSD([sQuery(id+"F16.wireOp",EDGE,"E439.sketch_text.stroke-0"),sQuery(id+"F16.wireOp",EDGE,"E439.sketch_text.stroke-1"),sQuery(id+"F16.wireOp",EDGE,"E439.sketch_text.stroke-2"),sQuery(id+"F16.wireOp",EDGE,"E439.sketch_text.stroke-3"),sQuery(id+"F16.wireOp",EDGE,"E439.sketch_text.stroke-4"),sQuery(id+"F16.wireOp",EDGE,"E439.sketch_text.stroke-5"),sQuery(id+"F16.wireOp",EDGE,"E439.sketch_text.stroke-6"),sQuery(id+"F16.wireOp",EDGE,"E439.sketch_text.stroke-7"),sQuery(id+"F16.wireOp",EDGE,"E439.sketch_text.stroke-8"),sQuery(id+"F16.wireOp",EDGE,"E439.sketch_text.stroke-9"),sQuery(id+"F16.wireOp",EDGE,"E439.sketch_text.stroke-10"),sQuery(id+"F16.wireOp",EDGE,"E439.sketch_text.stroke-11"),sQuery(id+"F16.wireOp",EDGE,"E439.sketch_text.stroke-12"),sQuery(id+"F16.wireOp",EDGE,"E439.sketch_text.stroke-13"),sQuery(id+"F16.wireOp",EDGE,"E439.sketch_text.stroke-14"),sQuery(id+"F16.wireOp",EDGE,"E439.sketch_text.stroke-15"),sQuery(id+"F16.wireOp",EDGE,"E439.sketch_text.stroke-16"),sQuery(id+"F16.wireOp",EDGE,"E439.sketch_text.stroke-17"),sQuery(id+"F16.wireOp",EDGE,"E439.sketch_text.stroke-18"),sQuery(id+"F16.wireOp",EDGE,"E439.sketch_text.stroke-19"),sQuery(id+"F16.wireOp",EDGE,"E439.sketch_text.stroke-20"),sQuery(id+"F16.wireOp",EDGE,"E439.sketch_text.stroke-21"),sQuery(id+"F16.wireOp",EDGE,"E439.sketch_text.stroke-22"),sQuery(id+"F16.wireOp",EDGE,"E439.sketch_text.stroke-23"),sQuery(id+"F16.wireOp",EDGE,"E439.sketch_text.stroke-24"),sQuery(id+"F16.wireOp",EDGE,"E439.sketch_text.stroke-25")])]});
            transform(context, id + "F18", {"entities" : qUnion([Q0]), "transformType" : TransformType.TRANSLATION_3D, "dx" : -15.1 * mm, "dy" : 0 * mm, "dz" : -6.1 * mm, "makeCopy" : false});
        }
        {
            var Q0;
            Q0=qCreatedBy(makeId("Front.planeOp"),FACE);
            var sketch = newSketch(context, id + "F19", { "sketchPlane" : qUnion([Q0])});
            skLineSegment(sketch, "E440.bottom", {"start": v(-55.74, 0) * mm, "end": v(83.96, 0) * mm});
            skLineSegment(sketch, "E440.top", {"start": v(-55.74, -3.7) * mm, "end": v(83.96, -3.7) * mm});
            skLineSegment(sketch, "E440.left", {"start": v(-55.74, 0) * mm, "end": v(-55.74, -3.7) * mm});
            skLineSegment(sketch, "E440.right", {"start": v(83.96, 0) * mm, "end": v(83.96, -3.7) * mm});
            skSolve(sketch);
        }
        {
            var Q0;
            Q0 = qSketchRegion(id + "F19", true);
            extrude(context, id + "F20", {"entities" : qUnion([Q0]), "operationType" : NewBodyOperationType.ADD, "depth" : 9.7 * mm, "offsetDistance" : 25 * mm});
        }
        {
            var Q0;
            Q0=makeQuery(id+"F20.opExtrude","CAP_EDGE",EDGE,{"disambiguationData":[OSD([sQuery(id+"F19.wireOp",EDGE,"E440.top")])],"isStart":false});
            chamfer(context, id + "F21", {"entities" : qUnion([Q0]), "width" : 4 * mm, "tangentPropagation" : true});
        }
        {
            var Q0;
            Q0=qCreatedBy(makeId("Front.planeOp"),FACE);
            var sketch = newSketch(context, id + "F22", { "sketchPlane" : qUnion([Q0])});
            skText(sketch, "E441", { "text": "ym", "fontName": "RobotoSlab-Bold.ttf"});
            const initialGuessF22  = {"E441": [0.01341, 0.0141, 1, 0, 0.01644]};
            skSetInitialGuess(sketch, initialGuessF22);
            skSolve(sketch);
        }
        {
            var Q0;
            Q0 = qSketchRegion(id + "F22", true);
            extrude(context, id + "F23", {"entities" : qUnion([Q0]), "depth" : 4.5 * mm, "offsetDistance" : 25 * mm});
        }
        {
            var Q0;
            Q0=makeQuery(id+"F23.opExtrude","SWEPT_BODY",BODY,{"disambiguationData":[OSD([sQuery(id+"F22.wireOp",EDGE,"E441.sketch_text.stroke-0"),sQuery(id+"F22.wireOp",EDGE,"E441.sketch_text.stroke-1"),sQuery(id+"F22.wireOp",EDGE,"E441.sketch_text.stroke-2"),sQuery(id+"F22.wireOp",EDGE,"E441.sketch_text.stroke-3"),sQuery(id+"F22.wireOp",EDGE,"E441.sketch_text.stroke-4"),sQuery(id+"F22.wireOp",EDGE,"E441.sketch_text.stroke-5"),sQuery(id+"F22.wireOp",EDGE,"E441.sketch_text.stroke-6"),sQuery(id+"F22.wireOp",EDGE,"E441.sketch_text.stroke-7"),sQuery(id+"F22.wireOp",EDGE,"E441.sketch_text.stroke-8"),sQuery(id+"F22.wireOp",EDGE,"E441.sketch_text.stroke-9"),sQuery(id+"F22.wireOp",EDGE,"E441.sketch_text.stroke-10"),sQuery(id+"F22.wireOp",EDGE,"E441.sketch_text.stroke-11"),sQuery(id+"F22.wireOp",EDGE,"E441.sketch_text.stroke-12"),sQuery(id+"F22.wireOp",EDGE,"E441.sketch_text.stroke-13"),sQuery(id+"F22.wireOp",EDGE,"E441.sketch_text.stroke-14"),sQuery(id+"F22.wireOp",EDGE,"E441.sketch_text.stroke-15"),sQuery(id+"F22.wireOp",EDGE,"E441.sketch_text.stroke-16"),sQuery(id+"F22.wireOp",EDGE,"E441.sketch_text.stroke-17"),sQuery(id+"F22.wireOp",EDGE,"E441.sketch_text.stroke-18"),sQuery(id+"F22.wireOp",EDGE,"E441.sketch_text.stroke-19"),sQuery(id+"F22.wireOp",EDGE,"E441.sketch_text.stroke-20"),sQuery(id+"F22.wireOp",EDGE,"E441.sketch_text.stroke-21"),sQuery(id+"F22.wireOp",EDGE,"E441.sketch_text.stroke-22"),sQuery(id+"F22.wireOp",EDGE,"E441.sketch_text.stroke-23"),sQuery(id+"F22.wireOp",EDGE,"E441.sketch_text.stroke-24"),sQuery(id+"F22.wireOp",EDGE,"E441.sketch_text.stroke-25")])]});
            transform(context, id + "F24", {"entities" : qUnion([Q0]), "transformType" : TransformType.TRANSLATION_3D, "dx" : -2.1 * mm, "dy" : 0 * mm, "dz" : 1.1 * mm, "makeCopy" : false});
        }
        {
            var Q0;
            Q0=makeQuery(id+"F23.opExtrude","SWEPT_BODY",BODY,{"disambiguationData":[OSD([sQuery(id+"F22.wireOp",EDGE,"E441.sketch_text.stroke-26"),sQuery(id+"F22.wireOp",EDGE,"E441.sketch_text.stroke-27"),sQuery(id+"F22.wireOp",EDGE,"E441.sketch_text.stroke-28"),sQuery(id+"F22.wireOp",EDGE,"E441.sketch_text.stroke-29"),sQuery(id+"F22.wireOp",EDGE,"E441.sketch_text.stroke-30"),sQuery(id+"F22.wireOp",EDGE,"E441.sketch_text.stroke-31"),sQuery(id+"F22.wireOp",EDGE,"E441.sketch_text.stroke-32"),sQuery(id+"F22.wireOp",EDGE,"E441.sketch_text.stroke-33"),sQuery(id+"F22.wireOp",EDGE,"E441.sketch_text.stroke-34"),sQuery(id+"F22.wireOp",EDGE,"E441.sketch_text.stroke-35"),sQuery(id+"F22.wireOp",EDGE,"E441.sketch_text.stroke-36"),sQuery(id+"F22.wireOp",EDGE,"E441.sketch_text.stroke-37"),sQuery(id+"F22.wireOp",EDGE,"E441.sketch_text.stroke-38"),sQuery(id+"F22.wireOp",EDGE,"E441.sketch_text.stroke-39"),sQuery(id+"F22.wireOp",EDGE,"E441.sketch_text.stroke-40"),sQuery(id+"F22.wireOp",EDGE,"E441.sketch_text.stroke-41"),sQuery(id+"F22.wireOp",EDGE,"E441.sketch_text.stroke-42"),sQuery(id+"F22.wireOp",EDGE,"E441.sketch_text.stroke-43"),sQuery(id+"F22.wireOp",EDGE,"E441.sketch_text.stroke-44"),sQuery(id+"F22.wireOp",EDGE,"E441.sketch_text.stroke-45"),sQuery(id+"F22.wireOp",EDGE,"E441.sketch_text.stroke-46"),sQuery(id+"F22.wireOp",EDGE,"E441.sketch_text.stroke-47"),sQuery(id+"F22.wireOp",EDGE,"E441.sketch_text.stroke-48"),sQuery(id+"F22.wireOp",EDGE,"E441.sketch_text.stroke-49"),sQuery(id+"F22.wireOp",EDGE,"E441.sketch_text.stroke-50"),sQuery(id+"F22.wireOp",EDGE,"E441.sketch_text.stroke-51"),sQuery(id+"F22.wireOp",EDGE,"E441.sketch_text.stroke-52"),sQuery(id+"F22.wireOp",EDGE,"E441.sketch_text.stroke-53"),sQuery(id+"F22.wireOp",EDGE,"E441.sketch_text.stroke-54"),sQuery(id+"F22.wireOp",EDGE,"E441.sketch_text.stroke-55"),sQuery(id+"F22.wireOp",EDGE,"E441.sketch_text.stroke-56"),sQuery(id+"F22.wireOp",EDGE,"E441.sketch_text.stroke-57"),sQuery(id+"F22.wireOp",EDGE,"E441.sketch_text.stroke-58"),sQuery(id+"F22.wireOp",EDGE,"E441.sketch_text.stroke-59"),sQuery(id+"F22.wireOp",EDGE,"E441.sketch_text.stroke-60"),sQuery(id+"F22.wireOp",EDGE,"E441.sketch_text.stroke-61"),sQuery(id+"F22.wireOp",EDGE,"E441.sketch_text.stroke-62"),sQuery(id+"F22.wireOp",EDGE,"E441.sketch_text.stroke-63"),sQuery(id+"F22.wireOp",EDGE,"E441.sketch_text.stroke-64"),sQuery(id+"F22.wireOp",EDGE,"E441.sketch_text.stroke-65"),sQuery(id+"F22.wireOp",EDGE,"E441.sketch_text.stroke-66"),sQuery(id+"F22.wireOp",EDGE,"E441.sketch_text.stroke-67"),sQuery(id+"F22.wireOp",EDGE,"E441.sketch_text.stroke-68")])]});
            transform(context, id + "F25", {"entities" : qUnion([Q0]), "transformType" : TransformType.TRANSLATION_3D, "dx" : -6.3 * mm, "dy" : 0 * mm, "dz" : -1.2 * mm, "makeCopy" : false});
        }
        {
            var Q0;
            Q0=makeQuery(id+"F23.opExtrude","CAP_FACE",FACE,{"disambiguationData":[OSD([sQuery(id+"F22.wireOp",EDGE,"E441.sketch_text.stroke-26"),sQuery(id+"F22.wireOp",EDGE,"E441.sketch_text.stroke-27"),sQuery(id+"F22.wireOp",EDGE,"E441.sketch_text.stroke-28"),sQuery(id+"F22.wireOp",EDGE,"E441.sketch_text.stroke-29"),sQuery(id+"F22.wireOp",EDGE,"E441.sketch_text.stroke-30"),sQuery(id+"F22.wireOp",EDGE,"E441.sketch_text.stroke-31"),sQuery(id+"F22.wireOp",EDGE,"E441.sketch_text.stroke-32"),sQuery(id+"F22.wireOp",EDGE,"E441.sketch_text.stroke-33"),sQuery(id+"F22.wireOp",EDGE,"E441.sketch_text.stroke-34"),sQuery(id+"F22.wireOp",EDGE,"E441.sketch_text.stroke-35"),sQuery(id+"F22.wireOp",EDGE,"E441.sketch_text.stroke-36"),sQuery(id+"F22.wireOp",EDGE,"E441.sketch_text.stroke-37"),sQuery(id+"F22.wireOp",EDGE,"E441.sketch_text.stroke-38"),sQuery(id+"F22.wireOp",EDGE,"E441.sketch_text.stroke-39"),sQuery(id+"F22.wireOp",EDGE,"E441.sketch_text.stroke-40"),sQuery(id+"F22.wireOp",EDGE,"E441.sketch_text.stroke-41"),sQuery(id+"F22.wireOp",EDGE,"E441.sketch_text.stroke-42"),sQuery(id+"F22.wireOp",EDGE,"E441.sketch_text.stroke-43"),sQuery(id+"F22.wireOp",EDGE,"E441.sketch_text.stroke-44"),sQuery(id+"F22.wireOp",EDGE,"E441.sketch_text.stroke-45"),sQuery(id+"F22.wireOp",EDGE,"E441.sketch_text.stroke-46"),sQuery(id+"F22.wireOp",EDGE,"E441.sketch_text.stroke-47"),sQuery(id+"F22.wireOp",EDGE,"E441.sketch_text.stroke-48"),sQuery(id+"F22.wireOp",EDGE,"E441.sketch_text.stroke-49"),sQuery(id+"F22.wireOp",EDGE,"E441.sketch_text.stroke-50"),sQuery(id+"F22.wireOp",EDGE,"E441.sketch_text.stroke-51"),sQuery(id+"F22.wireOp",EDGE,"E441.sketch_text.stroke-52"),sQuery(id+"F22.wireOp",EDGE,"E441.sketch_text.stroke-53"),sQuery(id+"F22.wireOp",EDGE,"E441.sketch_text.stroke-54"),sQuery(id+"F22.wireOp",EDGE,"E441.sketch_text.stroke-55"),sQuery(id+"F22.wireOp",EDGE,"E441.sketch_text.stroke-56"),sQuery(id+"F22.wireOp",EDGE,"E441.sketch_text.stroke-57"),sQuery(id+"F22.wireOp",EDGE,"E441.sketch_text.stroke-58"),sQuery(id+"F22.wireOp",EDGE,"E441.sketch_text.stroke-59"),sQuery(id+"F22.wireOp",EDGE,"E441.sketch_text.stroke-60"),sQuery(id+"F22.wireOp",EDGE,"E441.sketch_text.stroke-61"),sQuery(id+"F22.wireOp",EDGE,"E441.sketch_text.stroke-62"),sQuery(id+"F22.wireOp",EDGE,"E441.sketch_text.stroke-63"),sQuery(id+"F22.wireOp",EDGE,"E441.sketch_text.stroke-64"),sQuery(id+"F22.wireOp",EDGE,"E441.sketch_text.stroke-65"),sQuery(id+"F22.wireOp",EDGE,"E441.sketch_text.stroke-66"),sQuery(id+"F22.wireOp",EDGE,"E441.sketch_text.stroke-67"),sQuery(id+"F22.wireOp",EDGE,"E441.sketch_text.stroke-68")])],"isStart":false});
            extrude(context, id + "F26", {"entities" : qUnion([Q0]), "operationType" : NewBodyOperationType.ADD, "depth" : 1 * mm, "offsetDistance" : 25 * mm});
        }
        {
            var Q0;
            Q0=qCreatedBy(makeId("Front.planeOp"),FACE);
            var sketch = newSketch(context, id + "F27", { "sketchPlane" : qUnion([Q0])});
            skText(sketch, "E442", { "text": "S", "fontName": "RobotoSlab-Bold.ttf"});
            const initialGuessF27  = {"E442": [0.0293, -0.00643, 1, 0, 0.02592]};
            skSetInitialGuess(sketch, initialGuessF27);
            skSolve(sketch);
        }
        {
            var Q0;
            Q0 = qSketchRegion(id + "F27", true);
            extrude(context, id + "F28", {"entities" : qUnion([Q0]), "depth" : 3 * mm, "offsetDistance" : 25 * mm});
        }
        {
            var Q0;
            Q0=makeQuery(id+"F28.opExtrude","SWEPT_BODY",BODY,{"disambiguationData":[OSD([sQuery(id+"F27.wireOp",EDGE,"E442.sketch_text.stroke-0"),sQuery(id+"F27.wireOp",EDGE,"E442.sketch_text.stroke-1"),sQuery(id+"F27.wireOp",EDGE,"E442.sketch_text.stroke-2"),sQuery(id+"F27.wireOp",EDGE,"E442.sketch_text.stroke-3"),sQuery(id+"F27.wireOp",EDGE,"E442.sketch_text.stroke-4"),sQuery(id+"F27.wireOp",EDGE,"E442.sketch_text.stroke-5"),sQuery(id+"F27.wireOp",EDGE,"E442.sketch_text.stroke-6"),sQuery(id+"F27.wireOp",EDGE,"E442.sketch_text.stroke-7"),sQuery(id+"F27.wireOp",EDGE,"E442.sketch_text.stroke-8"),sQuery(id+"F27.wireOp",EDGE,"E442.sketch_text.stroke-9"),sQuery(id+"F27.wireOp",EDGE,"E442.sketch_text.stroke-10"),sQuery(id+"F27.wireOp",EDGE,"E442.sketch_text.stroke-11"),sQuery(id+"F27.wireOp",EDGE,"E442.sketch_text.stroke-12"),sQuery(id+"F27.wireOp",EDGE,"E442.sketch_text.stroke-13"),sQuery(id+"F27.wireOp",EDGE,"E442.sketch_text.stroke-14"),sQuery(id+"F27.wireOp",EDGE,"E442.sketch_text.stroke-15"),sQuery(id+"F27.wireOp",EDGE,"E442.sketch_text.stroke-16"),sQuery(id+"F27.wireOp",EDGE,"E442.sketch_text.stroke-17"),sQuery(id+"F27.wireOp",EDGE,"E442.sketch_text.stroke-18"),sQuery(id+"F27.wireOp",EDGE,"E442.sketch_text.stroke-19"),sQuery(id+"F27.wireOp",EDGE,"E442.sketch_text.stroke-20"),sQuery(id+"F27.wireOp",EDGE,"E442.sketch_text.stroke-21"),sQuery(id+"F27.wireOp",EDGE,"E442.sketch_text.stroke-22"),sQuery(id+"F27.wireOp",EDGE,"E442.sketch_text.stroke-23"),sQuery(id+"F27.wireOp",EDGE,"E442.sketch_text.stroke-24"),sQuery(id+"F27.wireOp",EDGE,"E442.sketch_text.stroke-25"),sQuery(id+"F27.wireOp",EDGE,"E442.sketch_text.stroke-26"),sQuery(id+"F27.wireOp",EDGE,"E442.sketch_text.stroke-27"),sQuery(id+"F27.wireOp",EDGE,"E442.sketch_text.stroke-28"),sQuery(id+"F27.wireOp",EDGE,"E442.sketch_text.stroke-29")])]});
            transform(context, id + "F29", {"entities" : qUnion([Q0]), "transformType" : TransformType.TRANSLATION_3D, "dx" : -4.7 * mm, "dy" : 0 * mm, "dz" : 5.7 * mm, "makeCopy" : false});
        }
        {
            var Q0;
            Q0=qCreatedBy(makeId("Front.planeOp"),FACE);
            var sketch = newSketch(context, id + "F30", { "sketchPlane" : qUnion([Q0])});
            skText(sketch, "E443", { "text": "tar", "fontName": "RobotoSlab-Bold.ttf"});
            const initialGuessF30  = {"E443": [0.04373, 0, 1, 0, 0.0125]};
            skSetInitialGuess(sketch, initialGuessF30);
            skSolve(sketch);
        }
        {
            var Q0;
            Q0 = qSketchRegion(id + "F30", true);
            extrude(context, id + "F31", {"entities" : qUnion([Q0]), "depth" : 3 * mm, "offsetDistance" : 25 * mm});
        }
        {
            var Q0;
            Q0=makeQuery(id+"F31.opExtrude","SWEPT_BODY",BODY,{"disambiguationData":[OSD([sQuery(id+"F30.wireOp",EDGE,"E443.sketch_text.stroke-0"),sQuery(id+"F30.wireOp",EDGE,"E443.sketch_text.stroke-1"),sQuery(id+"F30.wireOp",EDGE,"E443.sketch_text.stroke-2"),sQuery(id+"F30.wireOp",EDGE,"E443.sketch_text.stroke-3"),sQuery(id+"F30.wireOp",EDGE,"E443.sketch_text.stroke-4"),sQuery(id+"F30.wireOp",EDGE,"E443.sketch_text.stroke-5"),sQuery(id+"F30.wireOp",EDGE,"E443.sketch_text.stroke-6"),sQuery(id+"F30.wireOp",EDGE,"E443.sketch_text.stroke-7"),sQuery(id+"F30.wireOp",EDGE,"E443.sketch_text.stroke-8"),sQuery(id+"F30.wireOp",EDGE,"E443.sketch_text.stroke-9"),sQuery(id+"F30.wireOp",EDGE,"E443.sketch_text.stroke-10"),sQuery(id+"F30.wireOp",EDGE,"E443.sketch_text.stroke-11"),sQuery(id+"F30.wireOp",EDGE,"E443.sketch_text.stroke-12"),sQuery(id+"F30.wireOp",EDGE,"E443.sketch_text.stroke-13"),sQuery(id+"F30.wireOp",EDGE,"E443.sketch_text.stroke-14"),sQuery(id+"F30.wireOp",EDGE,"E443.sketch_text.stroke-15"),sQuery(id+"F30.wireOp",EDGE,"E443.sketch_text.stroke-16"),sQuery(id+"F30.wireOp",EDGE,"E443.sketch_text.stroke-17"),sQuery(id+"F30.wireOp",EDGE,"E443.sketch_text.stroke-18"),sQuery(id+"F30.wireOp",EDGE,"E443.sketch_text.stroke-19")])]});
            var Q1;
            Q1=makeQuery(id+"F31.opExtrude","SWEPT_BODY",BODY,{"disambiguationData":[OSD([sQuery(id+"F30.wireOp",EDGE,"E443.sketch_text.stroke-20"),sQuery(id+"F30.wireOp",EDGE,"E443.sketch_text.stroke-21"),sQuery(id+"F30.wireOp",EDGE,"E443.sketch_text.stroke-22"),sQuery(id+"F30.wireOp",EDGE,"E443.sketch_text.stroke-23"),sQuery(id+"F30.wireOp",EDGE,"E443.sketch_text.stroke-24"),sQuery(id+"F30.wireOp",EDGE,"E443.sketch_text.stroke-25"),sQuery(id+"F30.wireOp",EDGE,"E443.sketch_text.stroke-26"),sQuery(id+"F30.wireOp",EDGE,"E443.sketch_text.stroke-27"),sQuery(id+"F30.wireOp",EDGE,"E443.sketch_text.stroke-28"),sQuery(id+"F30.wireOp",EDGE,"E443.sketch_text.stroke-29"),sQuery(id+"F30.wireOp",EDGE,"E443.sketch_text.stroke-30"),sQuery(id+"F30.wireOp",EDGE,"E443.sketch_text.stroke-31"),sQuery(id+"F30.wireOp",EDGE,"E443.sketch_text.stroke-32"),sQuery(id+"F30.wireOp",EDGE,"E443.sketch_text.stroke-33"),sQuery(id+"F30.wireOp",EDGE,"E443.sketch_text.stroke-34"),sQuery(id+"F30.wireOp",EDGE,"E443.sketch_text.stroke-35"),sQuery(id+"F30.wireOp",EDGE,"E443.sketch_text.stroke-36"),sQuery(id+"F30.wireOp",EDGE,"E443.sketch_text.stroke-37"),sQuery(id+"F30.wireOp",EDGE,"E443.sketch_text.stroke-38"),sQuery(id+"F30.wireOp",EDGE,"E443.sketch_text.stroke-39"),sQuery(id+"F30.wireOp",EDGE,"E443.sketch_text.stroke-40"),sQuery(id+"F30.wireOp",EDGE,"E443.sketch_text.stroke-41"),sQuery(id+"F30.wireOp",EDGE,"E443.sketch_text.stroke-42"),sQuery(id+"F30.wireOp",EDGE,"E443.sketch_text.stroke-43"),sQuery(id+"F30.wireOp",EDGE,"E443.sketch_text.stroke-44"),sQuery(id+"F30.wireOp",EDGE,"E443.sketch_text.stroke-45"),sQuery(id+"F30.wireOp",EDGE,"E443.sketch_text.stroke-46"),sQuery(id+"F30.wireOp",EDGE,"E443.sketch_text.stroke-47"),sQuery(id+"F30.wireOp",EDGE,"E443.sketch_text.stroke-48"),sQuery(id+"F30.wireOp",EDGE,"E443.sketch_text.stroke-49"),sQuery(id+"F30.wireOp",EDGE,"E443.sketch_text.stroke-50"),sQuery(id+"F30.wireOp",EDGE,"E443.sketch_text.stroke-51"),sQuery(id+"F30.wireOp",EDGE,"E443.sketch_text.stroke-52"),sQuery(id+"F30.wireOp",EDGE,"E443.sketch_text.stroke-53"),sQuery(id+"F30.wireOp",EDGE,"E443.sketch_text.stroke-54")])]});
            var Q2;
            Q2=makeQuery(id+"F31.opExtrude","SWEPT_BODY",BODY,{"disambiguationData":[OSD([sQuery(id+"F30.wireOp",EDGE,"E443.sketch_text.stroke-55"),sQuery(id+"F30.wireOp",EDGE,"E443.sketch_text.stroke-56"),sQuery(id+"F30.wireOp",EDGE,"E443.sketch_text.stroke-57"),sQuery(id+"F30.wireOp",EDGE,"E443.sketch_text.stroke-58"),sQuery(id+"F30.wireOp",EDGE,"E443.sketch_text.stroke-59"),sQuery(id+"F30.wireOp",EDGE,"E443.sketch_text.stroke-60"),sQuery(id+"F30.wireOp",EDGE,"E443.sketch_text.stroke-61"),sQuery(id+"F30.wireOp",EDGE,"E443.sketch_text.stroke-62"),sQuery(id+"F30.wireOp",EDGE,"E443.sketch_text.stroke-63"),sQuery(id+"F30.wireOp",EDGE,"E443.sketch_text.stroke-64"),sQuery(id+"F30.wireOp",EDGE,"E443.sketch_text.stroke-65"),sQuery(id+"F30.wireOp",EDGE,"E443.sketch_text.stroke-66"),sQuery(id+"F30.wireOp",EDGE,"E443.sketch_text.stroke-67"),sQuery(id+"F30.wireOp",EDGE,"E443.sketch_text.stroke-68"),sQuery(id+"F30.wireOp",EDGE,"E443.sketch_text.stroke-69"),sQuery(id+"F30.wireOp",EDGE,"E443.sketch_text.stroke-70"),sQuery(id+"F30.wireOp",EDGE,"E443.sketch_text.stroke-71"),sQuery(id+"F30.wireOp",EDGE,"E443.sketch_text.stroke-72"),sQuery(id+"F30.wireOp",EDGE,"E443.sketch_text.stroke-73")])]});
            transform(context, id + "F32", {"entities" : qUnion([Q0, Q1, Q2]), "transformType" : TransformType.TRANSLATION_3D, "dx" : 1.3 * mm, "dy" : 0 * mm, "dz" : 0 * mm, "makeCopy" : false});
        }
        {
            var Q0;
            Q0=makeQuery(id+"F23.opExtrude","SWEPT_BODY",BODY,{"disambiguationData":[OSD([sQuery(id+"F22.wireOp",EDGE,"E441.sketch_text.stroke-0"),sQuery(id+"F22.wireOp",EDGE,"E441.sketch_text.stroke-1"),sQuery(id+"F22.wireOp",EDGE,"E441.sketch_text.stroke-2"),sQuery(id+"F22.wireOp",EDGE,"E441.sketch_text.stroke-3"),sQuery(id+"F22.wireOp",EDGE,"E441.sketch_text.stroke-4"),sQuery(id+"F22.wireOp",EDGE,"E441.sketch_text.stroke-5"),sQuery(id+"F22.wireOp",EDGE,"E441.sketch_text.stroke-6"),sQuery(id+"F22.wireOp",EDGE,"E441.sketch_text.stroke-7"),sQuery(id+"F22.wireOp",EDGE,"E441.sketch_text.stroke-8"),sQuery(id+"F22.wireOp",EDGE,"E441.sketch_text.stroke-9"),sQuery(id+"F22.wireOp",EDGE,"E441.sketch_text.stroke-10"),sQuery(id+"F22.wireOp",EDGE,"E441.sketch_text.stroke-11"),sQuery(id+"F22.wireOp",EDGE,"E441.sketch_text.stroke-12"),sQuery(id+"F22.wireOp",EDGE,"E441.sketch_text.stroke-13"),sQuery(id+"F22.wireOp",EDGE,"E441.sketch_text.stroke-14"),sQuery(id+"F22.wireOp",EDGE,"E441.sketch_text.stroke-15"),sQuery(id+"F22.wireOp",EDGE,"E441.sketch_text.stroke-16"),sQuery(id+"F22.wireOp",EDGE,"E441.sketch_text.stroke-17"),sQuery(id+"F22.wireOp",EDGE,"E441.sketch_text.stroke-18"),sQuery(id+"F22.wireOp",EDGE,"E441.sketch_text.stroke-19"),sQuery(id+"F22.wireOp",EDGE,"E441.sketch_text.stroke-20"),sQuery(id+"F22.wireOp",EDGE,"E441.sketch_text.stroke-21"),sQuery(id+"F22.wireOp",EDGE,"E441.sketch_text.stroke-22"),sQuery(id+"F22.wireOp",EDGE,"E441.sketch_text.stroke-23"),sQuery(id+"F22.wireOp",EDGE,"E441.sketch_text.stroke-24"),sQuery(id+"F22.wireOp",EDGE,"E441.sketch_text.stroke-25")])]});
            transform(context, id + "F33", {"entities" : qUnion([Q0]), "transformType" : TransformType.TRANSLATION_3D, "dx" : 0 * mm, "dy" : 0 * mm, "dz" : -2.7 * mm, "makeCopy" : false});
        }
        {
            var Q0;
            Q0=makeQuery(id+"F31.opExtrude","SWEPT_BODY",BODY,{"disambiguationData":[OSD([sQuery(id+"F30.wireOp",EDGE,"E443.sketch_text.stroke-55"),sQuery(id+"F30.wireOp",EDGE,"E443.sketch_text.stroke-56"),sQuery(id+"F30.wireOp",EDGE,"E443.sketch_text.stroke-57"),sQuery(id+"F30.wireOp",EDGE,"E443.sketch_text.stroke-58"),sQuery(id+"F30.wireOp",EDGE,"E443.sketch_text.stroke-59"),sQuery(id+"F30.wireOp",EDGE,"E443.sketch_text.stroke-60"),sQuery(id+"F30.wireOp",EDGE,"E443.sketch_text.stroke-61"),sQuery(id+"F30.wireOp",EDGE,"E443.sketch_text.stroke-62"),sQuery(id+"F30.wireOp",EDGE,"E443.sketch_text.stroke-63"),sQuery(id+"F30.wireOp",EDGE,"E443.sketch_text.stroke-64"),sQuery(id+"F30.wireOp",EDGE,"E443.sketch_text.stroke-65"),sQuery(id+"F30.wireOp",EDGE,"E443.sketch_text.stroke-66"),sQuery(id+"F30.wireOp",EDGE,"E443.sketch_text.stroke-67"),sQuery(id+"F30.wireOp",EDGE,"E443.sketch_text.stroke-68"),sQuery(id+"F30.wireOp",EDGE,"E443.sketch_text.stroke-69"),sQuery(id+"F30.wireOp",EDGE,"E443.sketch_text.stroke-70"),sQuery(id+"F30.wireOp",EDGE,"E443.sketch_text.stroke-71"),sQuery(id+"F30.wireOp",EDGE,"E443.sketch_text.stroke-72"),sQuery(id+"F30.wireOp",EDGE,"E443.sketch_text.stroke-73")])]});
            var Q1;
            Q1=makeQuery(id+"F31.opExtrude","SWEPT_BODY",BODY,{"disambiguationData":[OSD([sQuery(id+"F30.wireOp",EDGE,"E443.sketch_text.stroke-20"),sQuery(id+"F30.wireOp",EDGE,"E443.sketch_text.stroke-21"),sQuery(id+"F30.wireOp",EDGE,"E443.sketch_text.stroke-22"),sQuery(id+"F30.wireOp",EDGE,"E443.sketch_text.stroke-23"),sQuery(id+"F30.wireOp",EDGE,"E443.sketch_text.stroke-24"),sQuery(id+"F30.wireOp",EDGE,"E443.sketch_text.stroke-25"),sQuery(id+"F30.wireOp",EDGE,"E443.sketch_text.stroke-26"),sQuery(id+"F30.wireOp",EDGE,"E443.sketch_text.stroke-27"),sQuery(id+"F30.wireOp",EDGE,"E443.sketch_text.stroke-28"),sQuery(id+"F30.wireOp",EDGE,"E443.sketch_text.stroke-29"),sQuery(id+"F30.wireOp",EDGE,"E443.sketch_text.stroke-30"),sQuery(id+"F30.wireOp",EDGE,"E443.sketch_text.stroke-31"),sQuery(id+"F30.wireOp",EDGE,"E443.sketch_text.stroke-32"),sQuery(id+"F30.wireOp",EDGE,"E443.sketch_text.stroke-33"),sQuery(id+"F30.wireOp",EDGE,"E443.sketch_text.stroke-34"),sQuery(id+"F30.wireOp",EDGE,"E443.sketch_text.stroke-35"),sQuery(id+"F30.wireOp",EDGE,"E443.sketch_text.stroke-36"),sQuery(id+"F30.wireOp",EDGE,"E443.sketch_text.stroke-37"),sQuery(id+"F30.wireOp",EDGE,"E443.sketch_text.stroke-38"),sQuery(id+"F30.wireOp",EDGE,"E443.sketch_text.stroke-39"),sQuery(id+"F30.wireOp",EDGE,"E443.sketch_text.stroke-40"),sQuery(id+"F30.wireOp",EDGE,"E443.sketch_text.stroke-41"),sQuery(id+"F30.wireOp",EDGE,"E443.sketch_text.stroke-42"),sQuery(id+"F30.wireOp",EDGE,"E443.sketch_text.stroke-43"),sQuery(id+"F30.wireOp",EDGE,"E443.sketch_text.stroke-44"),sQuery(id+"F30.wireOp",EDGE,"E443.sketch_text.stroke-45"),sQuery(id+"F30.wireOp",EDGE,"E443.sketch_text.stroke-46"),sQuery(id+"F30.wireOp",EDGE,"E443.sketch_text.stroke-47"),sQuery(id+"F30.wireOp",EDGE,"E443.sketch_text.stroke-48"),sQuery(id+"F30.wireOp",EDGE,"E443.sketch_text.stroke-49"),sQuery(id+"F30.wireOp",EDGE,"E443.sketch_text.stroke-50"),sQuery(id+"F30.wireOp",EDGE,"E443.sketch_text.stroke-51"),sQuery(id+"F30.wireOp",EDGE,"E443.sketch_text.stroke-52"),sQuery(id+"F30.wireOp",EDGE,"E443.sketch_text.stroke-53"),sQuery(id+"F30.wireOp",EDGE,"E443.sketch_text.stroke-54")])]});
            var Q2;
            Q2=makeQuery(id+"F31.opExtrude","SWEPT_BODY",BODY,{"disambiguationData":[OSD([sQuery(id+"F30.wireOp",EDGE,"E443.sketch_text.stroke-0"),sQuery(id+"F30.wireOp",EDGE,"E443.sketch_text.stroke-1"),sQuery(id+"F30.wireOp",EDGE,"E443.sketch_text.stroke-2"),sQuery(id+"F30.wireOp",EDGE,"E443.sketch_text.stroke-3"),sQuery(id+"F30.wireOp",EDGE,"E443.sketch_text.stroke-4"),sQuery(id+"F30.wireOp",EDGE,"E443.sketch_text.stroke-5"),sQuery(id+"F30.wireOp",EDGE,"E443.sketch_text.stroke-6"),sQuery(id+"F30.wireOp",EDGE,"E443.sketch_text.stroke-7"),sQuery(id+"F30.wireOp",EDGE,"E443.sketch_text.stroke-8"),sQuery(id+"F30.wireOp",EDGE,"E443.sketch_text.stroke-9"),sQuery(id+"F30.wireOp",EDGE,"E443.sketch_text.stroke-10"),sQuery(id+"F30.wireOp",EDGE,"E443.sketch_text.stroke-11"),sQuery(id+"F30.wireOp",EDGE,"E443.sketch_text.stroke-12"),sQuery(id+"F30.wireOp",EDGE,"E443.sketch_text.stroke-13"),sQuery(id+"F30.wireOp",EDGE,"E443.sketch_text.stroke-14"),sQuery(id+"F30.wireOp",EDGE,"E443.sketch_text.stroke-15"),sQuery(id+"F30.wireOp",EDGE,"E443.sketch_text.stroke-16"),sQuery(id+"F30.wireOp",EDGE,"E443.sketch_text.stroke-17"),sQuery(id+"F30.wireOp",EDGE,"E443.sketch_text.stroke-18"),sQuery(id+"F30.wireOp",EDGE,"E443.sketch_text.stroke-19")])]});
            var Q3;
            Q3=makeQuery(id+"F28.opExtrude","SWEPT_BODY",BODY,{"disambiguationData":[OSD([sQuery(id+"F27.wireOp",EDGE,"E442.sketch_text.stroke-0"),sQuery(id+"F27.wireOp",EDGE,"E442.sketch_text.stroke-1"),sQuery(id+"F27.wireOp",EDGE,"E442.sketch_text.stroke-2"),sQuery(id+"F27.wireOp",EDGE,"E442.sketch_text.stroke-3"),sQuery(id+"F27.wireOp",EDGE,"E442.sketch_text.stroke-4"),sQuery(id+"F27.wireOp",EDGE,"E442.sketch_text.stroke-5"),sQuery(id+"F27.wireOp",EDGE,"E442.sketch_text.stroke-6"),sQuery(id+"F27.wireOp",EDGE,"E442.sketch_text.stroke-7"),sQuery(id+"F27.wireOp",EDGE,"E442.sketch_text.stroke-8"),sQuery(id+"F27.wireOp",EDGE,"E442.sketch_text.stroke-9"),sQuery(id+"F27.wireOp",EDGE,"E442.sketch_text.stroke-10"),sQuery(id+"F27.wireOp",EDGE,"E442.sketch_text.stroke-11"),sQuery(id+"F27.wireOp",EDGE,"E442.sketch_text.stroke-12"),sQuery(id+"F27.wireOp",EDGE,"E442.sketch_text.stroke-13"),sQuery(id+"F27.wireOp",EDGE,"E442.sketch_text.stroke-14"),sQuery(id+"F27.wireOp",EDGE,"E442.sketch_text.stroke-15"),sQuery(id+"F27.wireOp",EDGE,"E442.sketch_text.stroke-16"),sQuery(id+"F27.wireOp",EDGE,"E442.sketch_text.stroke-17"),sQuery(id+"F27.wireOp",EDGE,"E442.sketch_text.stroke-18"),sQuery(id+"F27.wireOp",EDGE,"E442.sketch_text.stroke-19"),sQuery(id+"F27.wireOp",EDGE,"E442.sketch_text.stroke-20"),sQuery(id+"F27.wireOp",EDGE,"E442.sketch_text.stroke-21"),sQuery(id+"F27.wireOp",EDGE,"E442.sketch_text.stroke-22"),sQuery(id+"F27.wireOp",EDGE,"E442.sketch_text.stroke-23"),sQuery(id+"F27.wireOp",EDGE,"E442.sketch_text.stroke-24"),sQuery(id+"F27.wireOp",EDGE,"E442.sketch_text.stroke-25"),sQuery(id+"F27.wireOp",EDGE,"E442.sketch_text.stroke-26"),sQuery(id+"F27.wireOp",EDGE,"E442.sketch_text.stroke-27"),sQuery(id+"F27.wireOp",EDGE,"E442.sketch_text.stroke-28"),sQuery(id+"F27.wireOp",EDGE,"E442.sketch_text.stroke-29")])]});
            var Q4;
            Q4=makeQuery(id+"F23.opExtrude","SWEPT_BODY",BODY,{"disambiguationData":[OSD([sQuery(id+"F22.wireOp",EDGE,"E441.sketch_text.stroke-26"),sQuery(id+"F22.wireOp",EDGE,"E441.sketch_text.stroke-27"),sQuery(id+"F22.wireOp",EDGE,"E441.sketch_text.stroke-28"),sQuery(id+"F22.wireOp",EDGE,"E441.sketch_text.stroke-29"),sQuery(id+"F22.wireOp",EDGE,"E441.sketch_text.stroke-30"),sQuery(id+"F22.wireOp",EDGE,"E441.sketch_text.stroke-31"),sQuery(id+"F22.wireOp",EDGE,"E441.sketch_text.stroke-32"),sQuery(id+"F22.wireOp",EDGE,"E441.sketch_text.stroke-33"),sQuery(id+"F22.wireOp",EDGE,"E441.sketch_text.stroke-34"),sQuery(id+"F22.wireOp",EDGE,"E441.sketch_text.stroke-35"),sQuery(id+"F22.wireOp",EDGE,"E441.sketch_text.stroke-36"),sQuery(id+"F22.wireOp",EDGE,"E441.sketch_text.stroke-37"),sQuery(id+"F22.wireOp",EDGE,"E441.sketch_text.stroke-38"),sQuery(id+"F22.wireOp",EDGE,"E441.sketch_text.stroke-39"),sQuery(id+"F22.wireOp",EDGE,"E441.sketch_text.stroke-40"),sQuery(id+"F22.wireOp",EDGE,"E441.sketch_text.stroke-41"),sQuery(id+"F22.wireOp",EDGE,"E441.sketch_text.stroke-42"),sQuery(id+"F22.wireOp",EDGE,"E441.sketch_text.stroke-43"),sQuery(id+"F22.wireOp",EDGE,"E441.sketch_text.stroke-44"),sQuery(id+"F22.wireOp",EDGE,"E441.sketch_text.stroke-45"),sQuery(id+"F22.wireOp",EDGE,"E441.sketch_text.stroke-46"),sQuery(id+"F22.wireOp",EDGE,"E441.sketch_text.stroke-47"),sQuery(id+"F22.wireOp",EDGE,"E441.sketch_text.stroke-48"),sQuery(id+"F22.wireOp",EDGE,"E441.sketch_text.stroke-49"),sQuery(id+"F22.wireOp",EDGE,"E441.sketch_text.stroke-50"),sQuery(id+"F22.wireOp",EDGE,"E441.sketch_text.stroke-51"),sQuery(id+"F22.wireOp",EDGE,"E441.sketch_text.stroke-52"),sQuery(id+"F22.wireOp",EDGE,"E441.sketch_text.stroke-53"),sQuery(id+"F22.wireOp",EDGE,"E441.sketch_text.stroke-54"),sQuery(id+"F22.wireOp",EDGE,"E441.sketch_text.stroke-55"),sQuery(id+"F22.wireOp",EDGE,"E441.sketch_text.stroke-56"),sQuery(id+"F22.wireOp",EDGE,"E441.sketch_text.stroke-57"),sQuery(id+"F22.wireOp",EDGE,"E441.sketch_text.stroke-58"),sQuery(id+"F22.wireOp",EDGE,"E441.sketch_text.stroke-59"),sQuery(id+"F22.wireOp",EDGE,"E441.sketch_text.stroke-60"),sQuery(id+"F22.wireOp",EDGE,"E441.sketch_text.stroke-61"),sQuery(id+"F22.wireOp",EDGE,"E441.sketch_text.stroke-62"),sQuery(id+"F22.wireOp",EDGE,"E441.sketch_text.stroke-63"),sQuery(id+"F22.wireOp",EDGE,"E441.sketch_text.stroke-64"),sQuery(id+"F22.wireOp",EDGE,"E441.sketch_text.stroke-65"),sQuery(id+"F22.wireOp",EDGE,"E441.sketch_text.stroke-66"),sQuery(id+"F22.wireOp",EDGE,"E441.sketch_text.stroke-67"),sQuery(id+"F22.wireOp",EDGE,"E441.sketch_text.stroke-68")])]});
            var Q5;
            Q5=makeQuery(id+"F23.opExtrude","SWEPT_BODY",BODY,{"disambiguationData":[OSD([sQuery(id+"F22.wireOp",EDGE,"E441.sketch_text.stroke-0"),sQuery(id+"F22.wireOp",EDGE,"E441.sketch_text.stroke-1"),sQuery(id+"F22.wireOp",EDGE,"E441.sketch_text.stroke-2"),sQuery(id+"F22.wireOp",EDGE,"E441.sketch_text.stroke-3"),sQuery(id+"F22.wireOp",EDGE,"E441.sketch_text.stroke-4"),sQuery(id+"F22.wireOp",EDGE,"E441.sketch_text.stroke-5"),sQuery(id+"F22.wireOp",EDGE,"E441.sketch_text.stroke-6"),sQuery(id+"F22.wireOp",EDGE,"E441.sketch_text.stroke-7"),sQuery(id+"F22.wireOp",EDGE,"E441.sketch_text.stroke-8"),sQuery(id+"F22.wireOp",EDGE,"E441.sketch_text.stroke-9"),sQuery(id+"F22.wireOp",EDGE,"E441.sketch_text.stroke-10"),sQuery(id+"F22.wireOp",EDGE,"E441.sketch_text.stroke-11"),sQuery(id+"F22.wireOp",EDGE,"E441.sketch_text.stroke-12"),sQuery(id+"F22.wireOp",EDGE,"E441.sketch_text.stroke-13"),sQuery(id+"F22.wireOp",EDGE,"E441.sketch_text.stroke-14"),sQuery(id+"F22.wireOp",EDGE,"E441.sketch_text.stroke-15"),sQuery(id+"F22.wireOp",EDGE,"E441.sketch_text.stroke-16"),sQuery(id+"F22.wireOp",EDGE,"E441.sketch_text.stroke-17"),sQuery(id+"F22.wireOp",EDGE,"E441.sketch_text.stroke-18"),sQuery(id+"F22.wireOp",EDGE,"E441.sketch_text.stroke-19"),sQuery(id+"F22.wireOp",EDGE,"E441.sketch_text.stroke-20"),sQuery(id+"F22.wireOp",EDGE,"E441.sketch_text.stroke-21"),sQuery(id+"F22.wireOp",EDGE,"E441.sketch_text.stroke-22"),sQuery(id+"F22.wireOp",EDGE,"E441.sketch_text.stroke-23"),sQuery(id+"F22.wireOp",EDGE,"E441.sketch_text.stroke-24"),sQuery(id+"F22.wireOp",EDGE,"E441.sketch_text.stroke-25")])]});
            var Q6;
            Q6=makeQuery(id+"F17.opExtrude","SWEPT_BODY",BODY,{"disambiguationData":[OSD([sQuery(id+"F16.wireOp",EDGE,"E439.sketch_text.stroke-0"),sQuery(id+"F16.wireOp",EDGE,"E439.sketch_text.stroke-1"),sQuery(id+"F16.wireOp",EDGE,"E439.sketch_text.stroke-2"),sQuery(id+"F16.wireOp",EDGE,"E439.sketch_text.stroke-3"),sQuery(id+"F16.wireOp",EDGE,"E439.sketch_text.stroke-4"),sQuery(id+"F16.wireOp",EDGE,"E439.sketch_text.stroke-5"),sQuery(id+"F16.wireOp",EDGE,"E439.sketch_text.stroke-6"),sQuery(id+"F16.wireOp",EDGE,"E439.sketch_text.stroke-7"),sQuery(id+"F16.wireOp",EDGE,"E439.sketch_text.stroke-8"),sQuery(id+"F16.wireOp",EDGE,"E439.sketch_text.stroke-9"),sQuery(id+"F16.wireOp",EDGE,"E439.sketch_text.stroke-10"),sQuery(id+"F16.wireOp",EDGE,"E439.sketch_text.stroke-11"),sQuery(id+"F16.wireOp",EDGE,"E439.sketch_text.stroke-12"),sQuery(id+"F16.wireOp",EDGE,"E439.sketch_text.stroke-13"),sQuery(id+"F16.wireOp",EDGE,"E439.sketch_text.stroke-14"),sQuery(id+"F16.wireOp",EDGE,"E439.sketch_text.stroke-15"),sQuery(id+"F16.wireOp",EDGE,"E439.sketch_text.stroke-16"),sQuery(id+"F16.wireOp",EDGE,"E439.sketch_text.stroke-17"),sQuery(id+"F16.wireOp",EDGE,"E439.sketch_text.stroke-18"),sQuery(id+"F16.wireOp",EDGE,"E439.sketch_text.stroke-19"),sQuery(id+"F16.wireOp",EDGE,"E439.sketch_text.stroke-20"),sQuery(id+"F16.wireOp",EDGE,"E439.sketch_text.stroke-21"),sQuery(id+"F16.wireOp",EDGE,"E439.sketch_text.stroke-22"),sQuery(id+"F16.wireOp",EDGE,"E439.sketch_text.stroke-23"),sQuery(id+"F16.wireOp",EDGE,"E439.sketch_text.stroke-24"),sQuery(id+"F16.wireOp",EDGE,"E439.sketch_text.stroke-25")])]});
            var Q7;
            Q7=makeQuery(id+"F7.opExtrude","SWEPT_BODY",BODY,{"disambiguationData":[OSD([sQuery(id+"F6.wireOp",EDGE,"E166"),sQuery(id+"F6.wireOp",EDGE,"E167"),sQuery(id+"F6.wireOp",EDGE,"E168"),sQuery(id+"F6.wireOp",EDGE,"E169"),sQuery(id+"F6.wireOp",EDGE,"E170"),sQuery(id+"F6.wireOp",EDGE,"E171"),sQuery(id+"F6.wireOp",EDGE,"E172"),sQuery(id+"F6.wireOp",EDGE,"E173"),sQuery(id+"F6.wireOp",EDGE,"E174"),sQuery(id+"F6.wireOp",EDGE,"E175"),sQuery(id+"F6.wireOp",EDGE,"E176"),sQuery(id+"F6.wireOp",EDGE,"E177"),sQuery(id+"F6.wireOp",EDGE,"E178"),sQuery(id+"F6.wireOp",EDGE,"E179"),sQuery(id+"F6.wireOp",EDGE,"E180"),sQuery(id+"F6.wireOp",EDGE,"E181"),sQuery(id+"F6.wireOp",EDGE,"E182"),sQuery(id+"F6.wireOp",EDGE,"E183"),sQuery(id+"F6.wireOp",EDGE,"E184"),sQuery(id+"F6.wireOp",EDGE,"E185"),sQuery(id+"F6.wireOp",EDGE,"E186"),sQuery(id+"F6.wireOp",EDGE,"E187"),sQuery(id+"F6.wireOp",EDGE,"E188"),sQuery(id+"F6.wireOp",EDGE,"E189"),sQuery(id+"F6.wireOp",EDGE,"E190"),sQuery(id+"F6.wireOp",EDGE,"E191"),sQuery(id+"F6.wireOp",EDGE,"E192"),sQuery(id+"F6.wireOp",EDGE,"E193"),sQuery(id+"F6.wireOp",EDGE,"E194"),sQuery(id+"F6.wireOp",EDGE,"E195"),sQuery(id+"F6.wireOp",EDGE,"E196"),sQuery(id+"F6.wireOp",EDGE,"E197"),sQuery(id+"F6.wireOp",EDGE,"E198"),sQuery(id+"F6.wireOp",EDGE,"E199"),sQuery(id+"F6.wireOp",EDGE,"E200"),sQuery(id+"F6.wireOp",EDGE,"E201"),sQuery(id+"F6.wireOp",EDGE,"E202"),sQuery(id+"F6.wireOp",EDGE,"E203"),sQuery(id+"F6.wireOp",EDGE,"E204"),sQuery(id+"F6.wireOp",EDGE,"E205"),sQuery(id+"F6.wireOp",EDGE,"E206"),sQuery(id+"F6.wireOp",EDGE,"E207"),sQuery(id+"F6.wireOp",EDGE,"E208"),sQuery(id+"F6.wireOp",EDGE,"E209"),sQuery(id+"F6.wireOp",EDGE,"E210"),sQuery(id+"F6.wireOp",EDGE,"E211"),sQuery(id+"F6.wireOp",EDGE,"E212"),sQuery(id+"F6.wireOp",EDGE,"E213"),sQuery(id+"F6.wireOp",EDGE,"E214"),sQuery(id+"F6.wireOp",EDGE,"E215"),sQuery(id+"F6.wireOp",EDGE,"E216"),sQuery(id+"F6.wireOp",EDGE,"E217"),sQuery(id+"F6.wireOp",EDGE,"E218"),sQuery(id+"F6.wireOp",EDGE,"E219"),sQuery(id+"F6.wireOp",EDGE,"E220"),sQuery(id+"F6.wireOp",EDGE,"E221"),sQuery(id+"F6.wireOp",EDGE,"E222"),sQuery(id+"F6.wireOp",EDGE,"E223"),sQuery(id+"F6.wireOp",EDGE,"E224"),sQuery(id+"F6.wireOp",EDGE,"E225"),sQuery(id+"F6.wireOp",EDGE,"E226"),sQuery(id+"F6.wireOp",EDGE,"E227"),sQuery(id+"F6.wireOp",EDGE,"E228"),sQuery(id+"F6.wireOp",EDGE,"E229"),sQuery(id+"F6.wireOp",EDGE,"E230"),sQuery(id+"F6.wireOp",EDGE,"E231"),sQuery(id+"F6.wireOp",EDGE,"E232"),sQuery(id+"F6.wireOp",EDGE,"E233"),sQuery(id+"F6.wireOp",EDGE,"E234"),sQuery(id+"F6.wireOp",EDGE,"E235"),sQuery(id+"F6.wireOp",EDGE,"E236"),sQuery(id+"F6.wireOp",EDGE,"E237"),sQuery(id+"F6.wireOp",EDGE,"E238"),sQuery(id+"F6.wireOp",EDGE,"E239"),sQuery(id+"F6.wireOp",EDGE,"E240"),sQuery(id+"F6.wireOp",EDGE,"E241"),sQuery(id+"F6.wireOp",EDGE,"E242"),sQuery(id+"F6.wireOp",EDGE,"E243"),sQuery(id+"F6.wireOp",EDGE,"E244"),sQuery(id+"F6.wireOp",EDGE,"E245"),sQuery(id+"F6.wireOp",EDGE,"E246"),sQuery(id+"F6.wireOp",EDGE,"E247"),sQuery(id+"F6.wireOp",EDGE,"E248"),sQuery(id+"F6.wireOp",EDGE,"E249"),sQuery(id+"F6.wireOp",EDGE,"E250")])]});
            var Q8;
            Q8=makeQuery(id+"F5.opExtrude","SWEPT_BODY",BODY,{"disambiguationData":[OSD([sQuery(id+"F4.wireOp",EDGE,"E141"),sQuery(id+"F4.wireOp",EDGE,"E142"),sQuery(id+"F4.wireOp",EDGE,"E143"),sQuery(id+"F4.wireOp",EDGE,"E144"),sQuery(id+"F4.wireOp",EDGE,"E145"),sQuery(id+"F4.wireOp",EDGE,"E146"),sQuery(id+"F4.wireOp",EDGE,"E147"),sQuery(id+"F4.wireOp",EDGE,"E148"),sQuery(id+"F4.wireOp",EDGE,"E149"),sQuery(id+"F4.wireOp",EDGE,"E150"),sQuery(id+"F4.wireOp",EDGE,"E151"),sQuery(id+"F4.wireOp",EDGE,"E152"),sQuery(id+"F4.wireOp",EDGE,"E153"),sQuery(id+"F4.wireOp",EDGE,"E154"),sQuery(id+"F4.wireOp",EDGE,"E155"),sQuery(id+"F4.wireOp",EDGE,"E156"),sQuery(id+"F4.wireOp",EDGE,"E157"),sQuery(id+"F4.wireOp",EDGE,"E158"),sQuery(id+"F4.wireOp",EDGE,"E159"),sQuery(id+"F4.wireOp",EDGE,"E160"),sQuery(id+"F4.wireOp",EDGE,"E161"),sQuery(id+"F4.wireOp",EDGE,"E162"),sQuery(id+"F4.wireOp",EDGE,"E163"),sQuery(id+"F4.wireOp",EDGE,"E164"),sQuery(id+"F4.wireOp",EDGE,"E165")])]});
            var Q9;
            Q9=makeQuery(id+"F3.opExtrude","SWEPT_BODY",BODY,{"disambiguationData":[OSD([sQuery(id+"F2.wireOp",EDGE,"E68"),sQuery(id+"F2.wireOp",EDGE,"E69"),sQuery(id+"F2.wireOp",EDGE,"E70"),sQuery(id+"F2.wireOp",EDGE,"E71"),sQuery(id+"F2.wireOp",EDGE,"E72"),sQuery(id+"F2.wireOp",EDGE,"E73"),sQuery(id+"F2.wireOp",EDGE,"E74"),sQuery(id+"F2.wireOp",EDGE,"E75"),sQuery(id+"F2.wireOp",EDGE,"E76"),sQuery(id+"F2.wireOp",EDGE,"E77"),sQuery(id+"F2.wireOp",EDGE,"E78"),sQuery(id+"F2.wireOp",EDGE,"E79"),sQuery(id+"F2.wireOp",EDGE,"E80"),sQuery(id+"F2.wireOp",EDGE,"E81"),sQuery(id+"F2.wireOp",EDGE,"E82"),sQuery(id+"F2.wireOp",EDGE,"E83"),sQuery(id+"F2.wireOp",EDGE,"E84"),sQuery(id+"F2.wireOp",EDGE,"E85"),sQuery(id+"F2.wireOp",EDGE,"E86"),sQuery(id+"F2.wireOp",EDGE,"E87"),sQuery(id+"F2.wireOp",EDGE,"E88"),sQuery(id+"F2.wireOp",EDGE,"E89"),sQuery(id+"F2.wireOp",EDGE,"E90"),sQuery(id+"F2.wireOp",EDGE,"E91"),sQuery(id+"F2.wireOp",EDGE,"E92"),sQuery(id+"F2.wireOp",EDGE,"E93"),sQuery(id+"F2.wireOp",EDGE,"E94"),sQuery(id+"F2.wireOp",EDGE,"E95"),sQuery(id+"F2.wireOp",EDGE,"E96"),sQuery(id+"F2.wireOp",EDGE,"E97"),sQuery(id+"F2.wireOp",EDGE,"E98"),sQuery(id+"F2.wireOp",EDGE,"E99"),sQuery(id+"F2.wireOp",EDGE,"E100"),sQuery(id+"F2.wireOp",EDGE,"E101"),sQuery(id+"F2.wireOp",EDGE,"E102"),sQuery(id+"F2.wireOp",EDGE,"E103"),sQuery(id+"F2.wireOp",EDGE,"E104"),sQuery(id+"F2.wireOp",EDGE,"E105"),sQuery(id+"F2.wireOp",EDGE,"E106"),sQuery(id+"F2.wireOp",EDGE,"E107"),sQuery(id+"F2.wireOp",EDGE,"E108"),sQuery(id+"F2.wireOp",EDGE,"E109"),sQuery(id+"F2.wireOp",EDGE,"E110"),sQuery(id+"F2.wireOp",EDGE,"E111"),sQuery(id+"F2.wireOp",EDGE,"E112"),sQuery(id+"F2.wireOp",EDGE,"E113"),sQuery(id+"F2.wireOp",EDGE,"E114"),sQuery(id+"F2.wireOp",EDGE,"E115"),sQuery(id+"F2.wireOp",EDGE,"E116"),sQuery(id+"F2.wireOp",EDGE,"E117"),sQuery(id+"F2.wireOp",EDGE,"E118"),sQuery(id+"F2.wireOp",EDGE,"E119"),sQuery(id+"F2.wireOp",EDGE,"E120"),sQuery(id+"F2.wireOp",EDGE,"E121"),sQuery(id+"F2.wireOp",EDGE,"E122"),sQuery(id+"F2.wireOp",EDGE,"E123"),sQuery(id+"F2.wireOp",EDGE,"E124"),sQuery(id+"F2.wireOp",EDGE,"E125"),sQuery(id+"F2.wireOp",EDGE,"E126"),sQuery(id+"F2.wireOp",EDGE,"E127"),sQuery(id+"F2.wireOp",EDGE,"E128"),sQuery(id+"F2.wireOp",EDGE,"E129"),sQuery(id+"F2.wireOp",EDGE,"E130"),sQuery(id+"F2.wireOp",EDGE,"E131"),sQuery(id+"F2.wireOp",EDGE,"E132"),sQuery(id+"F2.wireOp",EDGE,"E133"),sQuery(id+"F2.wireOp",EDGE,"E134"),sQuery(id+"F2.wireOp",EDGE,"E135"),sQuery(id+"F2.wireOp",EDGE,"E136"),sQuery(id+"F2.wireOp",EDGE,"E137"),sQuery(id+"F2.wireOp",EDGE,"E138"),sQuery(id+"F2.wireOp",EDGE,"E139"),sQuery(id+"F2.wireOp",EDGE,"E140")])]});
            var Q10;
            Q10=makeQuery(id+"F1.opExtrude","SWEPT_BODY",BODY,{"disambiguationData":[OSD([sQuery(id+"F0.wireOp",EDGE,"E0"),sQuery(id+"F0.wireOp",EDGE,"E1"),sQuery(id+"F0.wireOp",EDGE,"E2"),sQuery(id+"F0.wireOp",EDGE,"E3"),sQuery(id+"F0.wireOp",EDGE,"E4"),sQuery(id+"F0.wireOp",EDGE,"E5"),sQuery(id+"F0.wireOp",EDGE,"E6"),sQuery(id+"F0.wireOp",EDGE,"E7"),sQuery(id+"F0.wireOp",EDGE,"E8"),sQuery(id+"F0.wireOp",EDGE,"E9"),sQuery(id+"F0.wireOp",EDGE,"E10"),sQuery(id+"F0.wireOp",EDGE,"E11"),sQuery(id+"F0.wireOp",EDGE,"E12"),sQuery(id+"F0.wireOp",EDGE,"E13"),sQuery(id+"F0.wireOp",EDGE,"E14"),sQuery(id+"F0.wireOp",EDGE,"E15"),sQuery(id+"F0.wireOp",EDGE,"E16"),sQuery(id+"F0.wireOp",EDGE,"E17"),sQuery(id+"F0.wireOp",EDGE,"E18"),sQuery(id+"F0.wireOp",EDGE,"E19"),sQuery(id+"F0.wireOp",EDGE,"E20"),sQuery(id+"F0.wireOp",EDGE,"E21"),sQuery(id+"F0.wireOp",EDGE,"E22"),sQuery(id+"F0.wireOp",EDGE,"E23"),sQuery(id+"F0.wireOp",EDGE,"E24"),sQuery(id+"F0.wireOp",EDGE,"E25"),sQuery(id+"F0.wireOp",EDGE,"E26"),sQuery(id+"F0.wireOp",EDGE,"E27"),sQuery(id+"F0.wireOp",EDGE,"E28"),sQuery(id+"F0.wireOp",EDGE,"E29"),sQuery(id+"F0.wireOp",EDGE,"E30"),sQuery(id+"F0.wireOp",EDGE,"E31"),sQuery(id+"F0.wireOp",EDGE,"E32"),sQuery(id+"F0.wireOp",EDGE,"E33"),sQuery(id+"F0.wireOp",EDGE,"E34"),sQuery(id+"F0.wireOp",EDGE,"E35"),sQuery(id+"F0.wireOp",EDGE,"E36"),sQuery(id+"F0.wireOp",EDGE,"E37"),sQuery(id+"F0.wireOp",EDGE,"E38"),sQuery(id+"F0.wireOp",EDGE,"E39"),sQuery(id+"F0.wireOp",EDGE,"E40"),sQuery(id+"F0.wireOp",EDGE,"E41"),sQuery(id+"F0.wireOp",EDGE,"E42"),sQuery(id+"F0.wireOp",EDGE,"E43"),sQuery(id+"F0.wireOp",EDGE,"E44"),sQuery(id+"F0.wireOp",EDGE,"E45"),sQuery(id+"F0.wireOp",EDGE,"E46"),sQuery(id+"F0.wireOp",EDGE,"E47"),sQuery(id+"F0.wireOp",EDGE,"E48"),sQuery(id+"F0.wireOp",EDGE,"E49"),sQuery(id+"F0.wireOp",EDGE,"E50"),sQuery(id+"F0.wireOp",EDGE,"E51"),sQuery(id+"F0.wireOp",EDGE,"E52"),sQuery(id+"F0.wireOp",EDGE,"E53"),sQuery(id+"F0.wireOp",EDGE,"E54"),sQuery(id+"F0.wireOp",EDGE,"E55"),sQuery(id+"F0.wireOp",EDGE,"E56"),sQuery(id+"F0.wireOp",EDGE,"E57"),sQuery(id+"F0.wireOp",EDGE,"E58"),sQuery(id+"F0.wireOp",EDGE,"E59"),sQuery(id+"F0.wireOp",EDGE,"E60"),sQuery(id+"F0.wireOp",EDGE,"E61"),sQuery(id+"F0.wireOp",EDGE,"E62"),sQuery(id+"F0.wireOp",EDGE,"E63"),sQuery(id+"F0.wireOp",EDGE,"E64"),sQuery(id+"F0.wireOp",EDGE,"E65"),sQuery(id+"F0.wireOp",EDGE,"E66"),sQuery(id+"F0.wireOp",EDGE,"E67")])]});
            var Q11;
            Q11=makeQuery(id+"F28.opExtrude","CAP_VERTEX",VERTEX,{"disambiguationData":[OSD([sQuery(id+"F27.wireOp",EDGE,"E442.sketch_text.stroke-11"),sQuery(id+"F27.wireOp",EDGE,"E442.sketch_text.stroke-12")])],"isStart":true});
            transform(context, id + "F34", {"entities" : qUnion([Q0, Q1, Q2, Q3, Q4, Q5, Q6, Q7, Q8, Q9, Q10]), "transformType" : TransformType.SCALE_UNIFORMLY, "scale" : .85, "scalePoint" : qUnion([Q11]), "makeCopy" : false});
        }
    });
